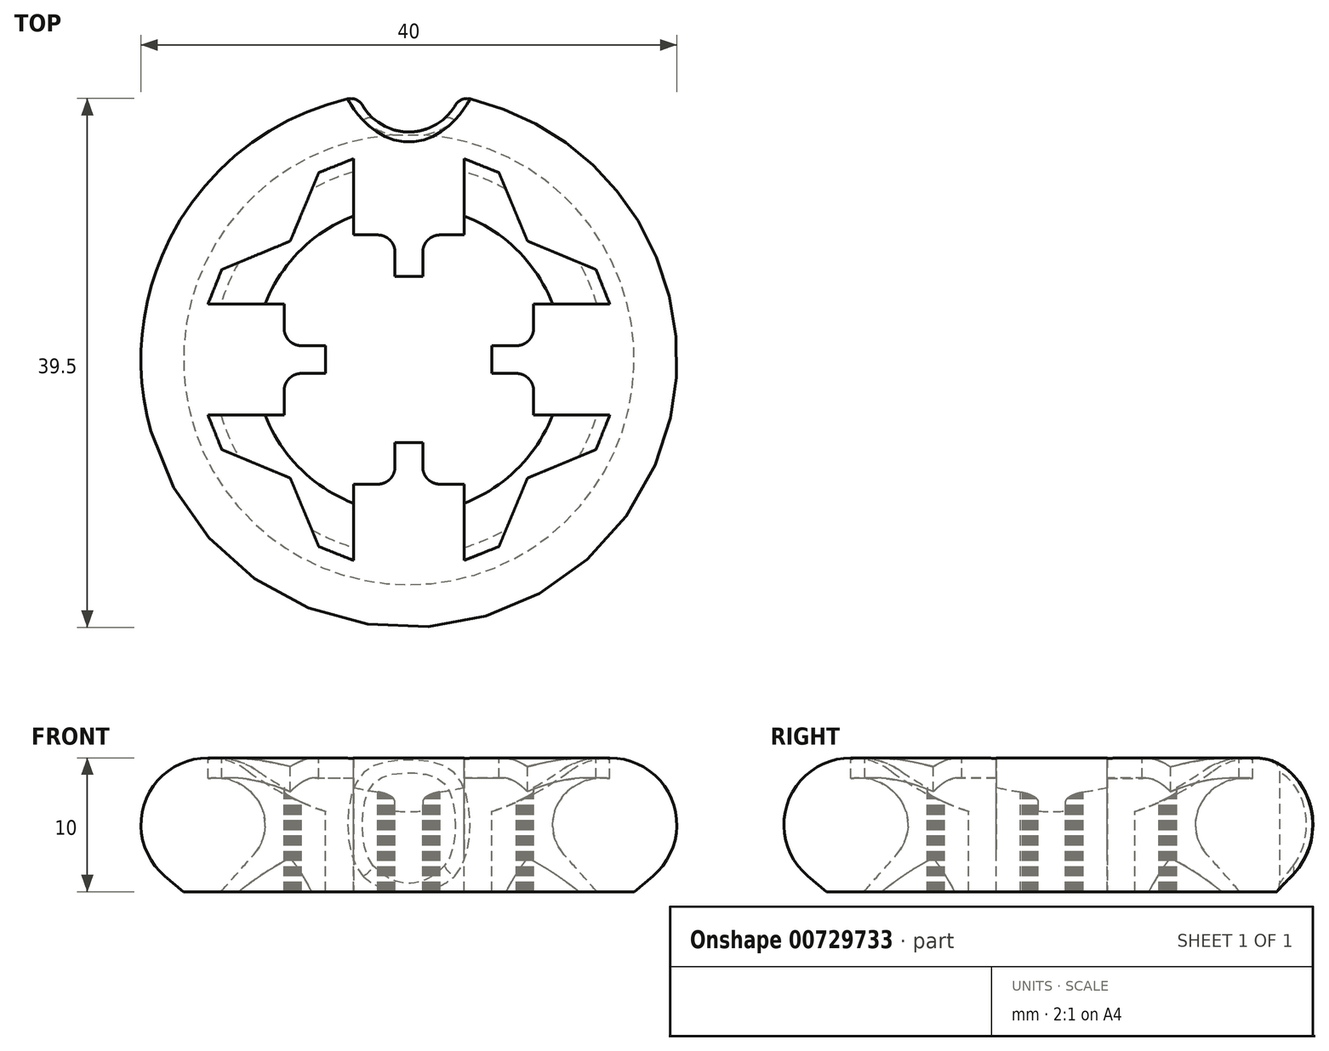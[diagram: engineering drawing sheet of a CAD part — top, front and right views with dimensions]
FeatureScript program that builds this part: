
annotation { "Feature Type Name" : "Feature", "Feature Type Description" : "" }
export const myFeature = defineFeature(function(context is Context, id is Id, definition is map)
    precondition{}
    {
        {
            var Q0;
            Q0=qCreatedBy(makeId("Front.planeOp"),FACE);
            var sketch = newSketch(context, id + "F0", { "sketchPlane" : qUnion([Q0])});
            skArc(sketch, "E0", {"start": v(-12, 9) * mm, "mid": v(-6.32, 6.03) * mm, "end": v(0, 5) * mm});
            skArc(sketch, "E1", {"start": v(-12, 9) * mm, "mid": v(-19.74, 6.58) * mm, "end": v(-15, 0) * mm});
            skLineSegment(sketch, "E2", {"start": v(0, 0) * mm, "end": v(-15, 0) * mm});
            skLineSegment(sketch, "E3", {"start": v(0, 0) * mm, "end": v(0, 5) * mm});
            skLineSegment(sketch, "E4", {"start": v(-18.21, 1.17) * mm, "end": v(-16.82, 0) * mm});
            skLineSegment(sketch, "E5", {"start": v(-16.82, 0) * mm, "end": v(-15, 0) * mm});
            skSolve(sketch);
        }
        {
            var Q0;
            Q0=qSketchRegion(id+"F0",true);
            var Q1;
            Q1=sQuery(id+"F0.wireOp",EDGE,"E3");
            revolve(context, id + "F1", {"surfaceOperationType" : NewSurfaceOperationType.NEW, "entities" : qUnion([Q0]), "axis" : qUnion([Q1]), "revolveType" : RevolveType.FULL});
        }
        {
            var Q0;
            Q0=qCreatedBy(makeId("Top.planeOp"),FACE);
            cPlane(context, id + "F2", {"entities" : qUnion([Q0]), "cplaneType" : CPlaneType.OFFSET, "offset" : 15 * mm, "width" : 150 * mm, "height" : 150 * mm});
        }
        {
            var Q0;
            Q0=qCreatedBy(id+"F2.planeOp",FACE);
            var sketch = newSketch(context, id + "F3", { "sketchPlane" : qUnion([Q0])});
            skLineSegment(sketch, "E6", {"start": v(9.31, -4.14) * mm, "end": v(9.31, -4.02) * mm});
            skLineSegment(sketch, "E7", {"start": v(9.31, -4.02) * mm, "end": v(9.31, -3.91) * mm});
            skLineSegment(sketch, "E8", {"start": v(9.31, -3.91) * mm, "end": v(9.31, -3.8) * mm});
            skLineSegment(sketch, "E9", {"start": v(9.31, -3.8) * mm, "end": v(9.31, -3.69) * mm});
            skLineSegment(sketch, "E10", {"start": v(9.31, -3.69) * mm, "end": v(9.31, -3.57) * mm});
            skLineSegment(sketch, "E11", {"start": v(9.31, -3.57) * mm, "end": v(9.31, -3.46) * mm});
            skLineSegment(sketch, "E12", {"start": v(9.31, -3.46) * mm, "end": v(9.31, -3.35) * mm});
            skLineSegment(sketch, "E13", {"start": v(9.31, -3.35) * mm, "end": v(9.31, -3.23) * mm});
            skLineSegment(sketch, "E14", {"start": v(9.31, -3.23) * mm, "end": v(9.31, -3.12) * mm});
            skLineSegment(sketch, "E15", {"start": v(9.31, -3.12) * mm, "end": v(9.31, -3) * mm});
            skLineSegment(sketch, "E16", {"start": v(9.31, -3) * mm, "end": v(9.31, -2.9) * mm});
            skLineSegment(sketch, "E17", {"start": v(9.31, -2.9) * mm, "end": v(9.31, -2.78) * mm});
            skLineSegment(sketch, "E18", {"start": v(9.31, -2.78) * mm, "end": v(9.31, -2.67) * mm});
            skLineSegment(sketch, "E19", {"start": v(9.31, -2.67) * mm, "end": v(9.31, -2.55) * mm});
            skLineSegment(sketch, "E20", {"start": v(9.31, -2.55) * mm, "end": v(9.31, -2.44) * mm});
            skLineSegment(sketch, "E21", {"start": v(9.31, -2.44) * mm, "end": v(9.31, -2.33) * mm});
            skLineSegment(sketch, "E22", {"start": v(9.31, -2.33) * mm, "end": v(9.3, -2.2) * mm});
            skLineSegment(sketch, "E23", {"start": v(9.3, -2.2) * mm, "end": v(9.28, -2.07) * mm});
            skLineSegment(sketch, "E24", {"start": v(9.28, -2.07) * mm, "end": v(9.25, -1.94) * mm});
            skLineSegment(sketch, "E25", {"start": v(9.25, -1.94) * mm, "end": v(9.2, -1.82) * mm});
            skLineSegment(sketch, "E26", {"start": v(9.2, -1.82) * mm, "end": v(9.15, -1.71) * mm});
            skLineSegment(sketch, "E27", {"start": v(9.15, -1.71) * mm, "end": v(9.09, -1.6) * mm});
            skLineSegment(sketch, "E28", {"start": v(9.09, -1.6) * mm, "end": v(9.02, -1.5) * mm});
            skLineSegment(sketch, "E29", {"start": v(9.02, -1.5) * mm, "end": v(8.93, -1.41) * mm});
            skLineSegment(sketch, "E30", {"start": v(8.93, -1.41) * mm, "end": v(8.84, -1.33) * mm});
            skLineSegment(sketch, "E31", {"start": v(8.84, -1.33) * mm, "end": v(8.74, -1.26) * mm});
            skLineSegment(sketch, "E32", {"start": v(8.74, -1.26) * mm, "end": v(8.63, -1.2) * mm});
            skLineSegment(sketch, "E33", {"start": v(8.63, -1.2) * mm, "end": v(8.52, -1.14) * mm});
            skLineSegment(sketch, "E34", {"start": v(8.52, -1.14) * mm, "end": v(8.4, -1.1) * mm});
            skLineSegment(sketch, "E35", {"start": v(8.4, -1.1) * mm, "end": v(8.28, -1.06) * mm});
            skLineSegment(sketch, "E36", {"start": v(8.28, -1.06) * mm, "end": v(8.15, -1.04) * mm});
            skLineSegment(sketch, "E37", {"start": v(8.15, -1.04) * mm, "end": v(8.02, -1.03) * mm});
            skLineSegment(sketch, "E38", {"start": v(8.02, -1.03) * mm, "end": v(7.9, -1.03) * mm});
            skLineSegment(sketch, "E39", {"start": v(7.9, -1.03) * mm, "end": v(7.8, -1.03) * mm});
            skLineSegment(sketch, "E40", {"start": v(7.8, -1.03) * mm, "end": v(7.68, -1.03) * mm});
            skLineSegment(sketch, "E41", {"start": v(7.68, -1.03) * mm, "end": v(7.56, -1.03) * mm});
            skLineSegment(sketch, "E42", {"start": v(7.56, -1.03) * mm, "end": v(7.45, -1.03) * mm});
            skLineSegment(sketch, "E43", {"start": v(7.45, -1.03) * mm, "end": v(7.34, -1.03) * mm});
            skLineSegment(sketch, "E44", {"start": v(7.34, -1.03) * mm, "end": v(7.23, -1.03) * mm});
            skLineSegment(sketch, "E45", {"start": v(7.23, -1.03) * mm, "end": v(7.11, -1.03) * mm});
            skLineSegment(sketch, "E46", {"start": v(7.11, -1.03) * mm, "end": v(7, -1.03) * mm});
            skLineSegment(sketch, "E47", {"start": v(7, -1.03) * mm, "end": v(6.89, -1.03) * mm});
            skLineSegment(sketch, "E48", {"start": v(6.89, -1.03) * mm, "end": v(6.77, -1.03) * mm});
            skLineSegment(sketch, "E49", {"start": v(6.77, -1.03) * mm, "end": v(6.66, -1.03) * mm});
            skLineSegment(sketch, "E50", {"start": v(6.66, -1.03) * mm, "end": v(6.55, -1.03) * mm});
            skLineSegment(sketch, "E51", {"start": v(6.55, -1.03) * mm, "end": v(6.43, -1.03) * mm});
            skLineSegment(sketch, "E52", {"start": v(6.43, -1.03) * mm, "end": v(6.32, -1.03) * mm});
            skLineSegment(sketch, "E53", {"start": v(6.32, -1.03) * mm, "end": v(6.2, -1.03) * mm});
            skLineSegment(sketch, "E54", {"start": v(6.2, -1.03) * mm, "end": v(6.2, -0.97) * mm});
            skLineSegment(sketch, "E55", {"start": v(6.2, -0.97) * mm, "end": v(6.2, -0.9) * mm});
            skLineSegment(sketch, "E56", {"start": v(6.2, -0.9) * mm, "end": v(6.2, -0.84) * mm});
            skLineSegment(sketch, "E57", {"start": v(6.2, -0.84) * mm, "end": v(6.2, -0.78) * mm});
            skLineSegment(sketch, "E58", {"start": v(6.2, -0.78) * mm, "end": v(6.2, -0.71) * mm});
            skLineSegment(sketch, "E59", {"start": v(6.2, -0.71) * mm, "end": v(6.2, -0.65) * mm});
            skLineSegment(sketch, "E60", {"start": v(6.2, -0.65) * mm, "end": v(6.2, -0.58) * mm});
            skLineSegment(sketch, "E61", {"start": v(6.2, -0.58) * mm, "end": v(6.2, -0.52) * mm});
            skLineSegment(sketch, "E62", {"start": v(6.2, -0.52) * mm, "end": v(6.2, -0.45) * mm});
            skLineSegment(sketch, "E63", {"start": v(6.2, -0.45) * mm, "end": v(6.2, -0.39) * mm});
            skLineSegment(sketch, "E64", {"start": v(6.2, -0.39) * mm, "end": v(6.2, -0.32) * mm});
            skLineSegment(sketch, "E65", {"start": v(6.2, -0.32) * mm, "end": v(6.2, -0.26) * mm});
            skLineSegment(sketch, "E66", {"start": v(6.2, -0.26) * mm, "end": v(6.2, -0.2) * mm});
            skLineSegment(sketch, "E67", {"start": v(6.2, -0.2) * mm, "end": v(6.2, -0.13) * mm});
            skLineSegment(sketch, "E68", {"start": v(6.2, -0.13) * mm, "end": v(6.2, -0.06) * mm});
            skLineSegment(sketch, "E69", {"start": v(6.2, -0.06) * mm, "end": v(6.2, 0) * mm});
            skLineSegment(sketch, "E70", {"start": v(6.2, 0) * mm, "end": v(6.2, 0.06) * mm});
            skLineSegment(sketch, "E71", {"start": v(6.2, 0.06) * mm, "end": v(6.2, 0.13) * mm});
            skLineSegment(sketch, "E72", {"start": v(6.2, 0.13) * mm, "end": v(6.2, 0.2) * mm});
            skLineSegment(sketch, "E73", {"start": v(6.2, 0.2) * mm, "end": v(6.2, 0.26) * mm});
            skLineSegment(sketch, "E74", {"start": v(6.2, 0.26) * mm, "end": v(6.2, 0.32) * mm});
            skLineSegment(sketch, "E75", {"start": v(6.2, 0.32) * mm, "end": v(6.2, 0.39) * mm});
            skLineSegment(sketch, "E76", {"start": v(6.2, 0.39) * mm, "end": v(6.2, 0.45) * mm});
            skLineSegment(sketch, "E77", {"start": v(6.2, 0.45) * mm, "end": v(6.2, 0.52) * mm});
            skLineSegment(sketch, "E78", {"start": v(6.2, 0.52) * mm, "end": v(6.2, 0.58) * mm});
            skLineSegment(sketch, "E79", {"start": v(6.2, 0.58) * mm, "end": v(6.2, 0.65) * mm});
            skLineSegment(sketch, "E80", {"start": v(6.2, 0.65) * mm, "end": v(6.2, 0.71) * mm});
            skLineSegment(sketch, "E81", {"start": v(6.2, 0.71) * mm, "end": v(6.2, 0.78) * mm});
            skLineSegment(sketch, "E82", {"start": v(6.2, 0.78) * mm, "end": v(6.2, 0.84) * mm});
            skLineSegment(sketch, "E83", {"start": v(6.2, 0.84) * mm, "end": v(6.2, 0.9) * mm});
            skLineSegment(sketch, "E84", {"start": v(6.2, 0.9) * mm, "end": v(6.2, 0.97) * mm});
            skLineSegment(sketch, "E85", {"start": v(6.2, 0.97) * mm, "end": v(6.2, 1.03) * mm});
            skLineSegment(sketch, "E86", {"start": v(6.2, 1.03) * mm, "end": v(6.32, 1.03) * mm});
            skLineSegment(sketch, "E87", {"start": v(6.32, 1.03) * mm, "end": v(6.43, 1.03) * mm});
            skLineSegment(sketch, "E88", {"start": v(6.43, 1.03) * mm, "end": v(6.55, 1.03) * mm});
            skLineSegment(sketch, "E89", {"start": v(6.55, 1.03) * mm, "end": v(6.66, 1.03) * mm});
            skLineSegment(sketch, "E90", {"start": v(6.66, 1.03) * mm, "end": v(6.77, 1.03) * mm});
            skLineSegment(sketch, "E91", {"start": v(6.77, 1.03) * mm, "end": v(6.89, 1.03) * mm});
            skLineSegment(sketch, "E92", {"start": v(6.89, 1.03) * mm, "end": v(7, 1.03) * mm});
            skLineSegment(sketch, "E93", {"start": v(7, 1.03) * mm, "end": v(7.11, 1.03) * mm});
            skLineSegment(sketch, "E94", {"start": v(7.11, 1.03) * mm, "end": v(7.23, 1.03) * mm});
            skLineSegment(sketch, "E95", {"start": v(7.23, 1.03) * mm, "end": v(7.34, 1.03) * mm});
            skLineSegment(sketch, "E96", {"start": v(7.34, 1.03) * mm, "end": v(7.45, 1.03) * mm});
            skLineSegment(sketch, "E97", {"start": v(7.45, 1.03) * mm, "end": v(7.56, 1.03) * mm});
            skLineSegment(sketch, "E98", {"start": v(7.56, 1.03) * mm, "end": v(7.68, 1.03) * mm});
            skLineSegment(sketch, "E99", {"start": v(7.68, 1.03) * mm, "end": v(7.8, 1.03) * mm});
            skLineSegment(sketch, "E100", {"start": v(7.8, 1.03) * mm, "end": v(7.9, 1.03) * mm});
            skLineSegment(sketch, "E101", {"start": v(7.9, 1.03) * mm, "end": v(8.02, 1.03) * mm});
            skLineSegment(sketch, "E102", {"start": v(8.02, 1.03) * mm, "end": v(8.15, 1.04) * mm});
            skLineSegment(sketch, "E103", {"start": v(8.15, 1.04) * mm, "end": v(8.28, 1.06) * mm});
            skLineSegment(sketch, "E104", {"start": v(8.28, 1.06) * mm, "end": v(8.4, 1.1) * mm});
            skLineSegment(sketch, "E105", {"start": v(8.4, 1.1) * mm, "end": v(8.52, 1.14) * mm});
            skLineSegment(sketch, "E106", {"start": v(8.52, 1.14) * mm, "end": v(8.63, 1.2) * mm});
            skLineSegment(sketch, "E107", {"start": v(8.63, 1.2) * mm, "end": v(8.74, 1.26) * mm});
            skLineSegment(sketch, "E108", {"start": v(8.74, 1.26) * mm, "end": v(8.84, 1.33) * mm});
            skLineSegment(sketch, "E109", {"start": v(8.84, 1.33) * mm, "end": v(8.93, 1.41) * mm});
            skLineSegment(sketch, "E110", {"start": v(8.93, 1.41) * mm, "end": v(9.02, 1.5) * mm});
            skLineSegment(sketch, "E111", {"start": v(9.02, 1.5) * mm, "end": v(9.09, 1.6) * mm});
            skLineSegment(sketch, "E112", {"start": v(9.09, 1.6) * mm, "end": v(9.15, 1.71) * mm});
            skLineSegment(sketch, "E113", {"start": v(9.15, 1.71) * mm, "end": v(9.2, 1.82) * mm});
            skLineSegment(sketch, "E114", {"start": v(9.2, 1.82) * mm, "end": v(9.25, 1.94) * mm});
            skLineSegment(sketch, "E115", {"start": v(9.25, 1.94) * mm, "end": v(9.28, 2.07) * mm});
            skLineSegment(sketch, "E116", {"start": v(9.28, 2.07) * mm, "end": v(9.3, 2.2) * mm});
            skLineSegment(sketch, "E117", {"start": v(9.3, 2.2) * mm, "end": v(9.31, 2.33) * mm});
            skLineSegment(sketch, "E118", {"start": v(9.31, 2.33) * mm, "end": v(9.31, 2.44) * mm});
            skLineSegment(sketch, "E119", {"start": v(9.31, 2.44) * mm, "end": v(9.31, 2.55) * mm});
            skLineSegment(sketch, "E120", {"start": v(9.31, 2.55) * mm, "end": v(9.31, 2.67) * mm});
            skLineSegment(sketch, "E121", {"start": v(9.31, 2.67) * mm, "end": v(9.31, 2.78) * mm});
            skLineSegment(sketch, "E122", {"start": v(9.31, 2.78) * mm, "end": v(9.31, 2.9) * mm});
            skLineSegment(sketch, "E123", {"start": v(9.31, 2.9) * mm, "end": v(9.31, 3) * mm});
            skLineSegment(sketch, "E124", {"start": v(9.31, 3) * mm, "end": v(9.31, 3.12) * mm});
            skLineSegment(sketch, "E125", {"start": v(9.31, 3.12) * mm, "end": v(9.31, 3.23) * mm});
            skLineSegment(sketch, "E126", {"start": v(9.31, 3.23) * mm, "end": v(9.31, 3.35) * mm});
            skLineSegment(sketch, "E127", {"start": v(9.31, 3.35) * mm, "end": v(9.31, 3.46) * mm});
            skLineSegment(sketch, "E128", {"start": v(9.31, 3.46) * mm, "end": v(9.31, 3.57) * mm});
            skLineSegment(sketch, "E129", {"start": v(9.31, 3.57) * mm, "end": v(9.31, 3.69) * mm});
            skLineSegment(sketch, "E130", {"start": v(9.31, 3.69) * mm, "end": v(9.31, 3.8) * mm});
            skLineSegment(sketch, "E131", {"start": v(9.31, 3.8) * mm, "end": v(9.31, 3.91) * mm});
            skLineSegment(sketch, "E132", {"start": v(9.31, 3.91) * mm, "end": v(9.31, 4.02) * mm});
            skLineSegment(sketch, "E133", {"start": v(9.31, 4.02) * mm, "end": v(9.31, 4.14) * mm});
            skLineSegment(sketch, "E134", {"start": v(9.31, 4.14) * mm, "end": v(9.44, 4.14) * mm});
            skLineSegment(sketch, "E135", {"start": v(9.44, 4.14) * mm, "end": v(9.57, 4.14) * mm});
            skLineSegment(sketch, "E136", {"start": v(9.57, 4.14) * mm, "end": v(9.7, 4.14) * mm});
            skLineSegment(sketch, "E137", {"start": v(9.7, 4.14) * mm, "end": v(9.83, 4.14) * mm});
            skLineSegment(sketch, "E138", {"start": v(9.83, 4.14) * mm, "end": v(9.96, 4.14) * mm});
            skLineSegment(sketch, "E139", {"start": v(9.96, 4.14) * mm, "end": v(10.09, 4.14) * mm});
            skLineSegment(sketch, "E140", {"start": v(10.09, 4.14) * mm, "end": v(10.22, 4.14) * mm});
            skLineSegment(sketch, "E141", {"start": v(10.22, 4.14) * mm, "end": v(10.34, 4.14) * mm});
            skLineSegment(sketch, "E142", {"start": v(10.34, 4.14) * mm, "end": v(10.47, 4.14) * mm});
            skLineSegment(sketch, "E143", {"start": v(10.47, 4.14) * mm, "end": v(10.6, 4.14) * mm});
            skLineSegment(sketch, "E144", {"start": v(10.6, 4.14) * mm, "end": v(10.73, 4.14) * mm});
            skLineSegment(sketch, "E145", {"start": v(10.73, 4.14) * mm, "end": v(10.86, 4.14) * mm});
            skLineSegment(sketch, "E146", {"start": v(10.86, 4.14) * mm, "end": v(11, 4.14) * mm});
            skLineSegment(sketch, "E147", {"start": v(11, 4.14) * mm, "end": v(11.12, 4.14) * mm});
            skLineSegment(sketch, "E148", {"start": v(11.12, 4.14) * mm, "end": v(11.25, 4.14) * mm});
            skLineSegment(sketch, "E149", {"start": v(11.25, 4.14) * mm, "end": v(11.38, 4.14) * mm});
            skLineSegment(sketch, "E150", {"start": v(11.38, 4.14) * mm, "end": v(11.6, 4.14) * mm});
            skLineSegment(sketch, "E151", {"start": v(11.6, 4.14) * mm, "end": v(11.83, 4.14) * mm});
            skLineSegment(sketch, "E152", {"start": v(11.83, 4.14) * mm, "end": v(12.06, 4.14) * mm});
            skLineSegment(sketch, "E153", {"start": v(12.06, 4.14) * mm, "end": v(12.28, 4.14) * mm});
            skLineSegment(sketch, "E154", {"start": v(12.28, 4.14) * mm, "end": v(12.51, 4.14) * mm});
            skLineSegment(sketch, "E155", {"start": v(12.51, 4.14) * mm, "end": v(12.74, 4.14) * mm});
            skLineSegment(sketch, "E156", {"start": v(12.74, 4.14) * mm, "end": v(12.96, 4.14) * mm});
            skLineSegment(sketch, "E157", {"start": v(12.96, 4.14) * mm, "end": v(13.19, 4.14) * mm});
            skLineSegment(sketch, "E158", {"start": v(13.19, 4.14) * mm, "end": v(13.42, 4.14) * mm});
            skLineSegment(sketch, "E159", {"start": v(13.42, 4.14) * mm, "end": v(13.64, 4.14) * mm});
            skLineSegment(sketch, "E160", {"start": v(13.64, 4.14) * mm, "end": v(13.87, 4.14) * mm});
            skLineSegment(sketch, "E161", {"start": v(13.87, 4.14) * mm, "end": v(14.1, 4.14) * mm});
            skLineSegment(sketch, "E162", {"start": v(14.1, 4.14) * mm, "end": v(14.32, 4.14) * mm});
            skLineSegment(sketch, "E163", {"start": v(14.32, 4.14) * mm, "end": v(14.55, 4.14) * mm});
            skLineSegment(sketch, "E164", {"start": v(14.55, 4.14) * mm, "end": v(14.77, 4.14) * mm});
            skLineSegment(sketch, "E165", {"start": v(14.77, 4.14) * mm, "end": v(15, 4.14) * mm});
            skLineSegment(sketch, "E166", {"start": v(15, 4.14) * mm, "end": v(14.95, 4.27) * mm});
            skLineSegment(sketch, "E167", {"start": v(14.95, 4.27) * mm, "end": v(14.9, 4.4) * mm});
            skLineSegment(sketch, "E168", {"start": v(14.9, 4.4) * mm, "end": v(14.84, 4.53) * mm});
            skLineSegment(sketch, "E169", {"start": v(14.84, 4.53) * mm, "end": v(14.8, 4.66) * mm});
            skLineSegment(sketch, "E170", {"start": v(14.8, 4.66) * mm, "end": v(14.74, 4.78) * mm});
            skLineSegment(sketch, "E171", {"start": v(14.74, 4.78) * mm, "end": v(14.69, 4.91) * mm});
            skLineSegment(sketch, "E172", {"start": v(14.69, 4.91) * mm, "end": v(14.64, 5.04) * mm});
            skLineSegment(sketch, "E173", {"start": v(14.64, 5.04) * mm, "end": v(14.59, 5.17) * mm});
            skLineSegment(sketch, "E174", {"start": v(14.59, 5.17) * mm, "end": v(14.53, 5.3) * mm});
            skLineSegment(sketch, "E175", {"start": v(14.53, 5.3) * mm, "end": v(14.48, 5.43) * mm});
            skLineSegment(sketch, "E176", {"start": v(14.48, 5.43) * mm, "end": v(14.43, 5.56) * mm});
            skLineSegment(sketch, "E177", {"start": v(14.43, 5.56) * mm, "end": v(14.38, 5.69) * mm});
            skLineSegment(sketch, "E178", {"start": v(14.38, 5.69) * mm, "end": v(14.33, 5.82) * mm});
            skLineSegment(sketch, "E179", {"start": v(14.33, 5.82) * mm, "end": v(14.28, 5.95) * mm});
            skLineSegment(sketch, "E180", {"start": v(14.28, 5.95) * mm, "end": v(14.22, 6.08) * mm});
            skLineSegment(sketch, "E181", {"start": v(14.22, 6.08) * mm, "end": v(14.17, 6.2) * mm});
            skLineSegment(sketch, "E182", {"start": v(14.17, 6.2) * mm, "end": v(14.16, 6.24) * mm});
            skLineSegment(sketch, "E183", {"start": v(14.16, 6.24) * mm, "end": v(14.15, 6.27) * mm});
            skLineSegment(sketch, "E184", {"start": v(14.15, 6.27) * mm, "end": v(14.13, 6.3) * mm});
            skLineSegment(sketch, "E185", {"start": v(14.13, 6.3) * mm, "end": v(14.12, 6.34) * mm});
            skLineSegment(sketch, "E186", {"start": v(14.12, 6.34) * mm, "end": v(14.1, 6.37) * mm});
            skLineSegment(sketch, "E187", {"start": v(14.1, 6.37) * mm, "end": v(14.1, 6.4) * mm});
            skLineSegment(sketch, "E188", {"start": v(14.1, 6.4) * mm, "end": v(14.08, 6.43) * mm});
            skLineSegment(sketch, "E189", {"start": v(14.08, 6.43) * mm, "end": v(14.07, 6.47) * mm});
            skLineSegment(sketch, "E190", {"start": v(14.07, 6.47) * mm, "end": v(14.06, 6.5) * mm});
            skLineSegment(sketch, "E191", {"start": v(14.06, 6.5) * mm, "end": v(14.04, 6.53) * mm});
            skLineSegment(sketch, "E192", {"start": v(14.04, 6.53) * mm, "end": v(14.03, 6.56) * mm});
            skLineSegment(sketch, "E193", {"start": v(14.03, 6.56) * mm, "end": v(14.02, 6.6) * mm});
            skLineSegment(sketch, "E194", {"start": v(14.02, 6.6) * mm, "end": v(14, 6.63) * mm});
            skLineSegment(sketch, "E195", {"start": v(14, 6.63) * mm, "end": v(14, 6.66) * mm});
            skLineSegment(sketch, "E196", {"start": v(14, 6.66) * mm, "end": v(13.98, 6.7) * mm});
            skLineSegment(sketch, "E197", {"start": v(13.98, 6.7) * mm, "end": v(13.97, 6.72) * mm});
            skLineSegment(sketch, "E198", {"start": v(13.97, 6.72) * mm, "end": v(13.65, 6.86) * mm});
            skLineSegment(sketch, "E199", {"start": v(13.65, 6.86) * mm, "end": v(13.33, 7) * mm});
            skLineSegment(sketch, "E200", {"start": v(13.33, 7) * mm, "end": v(13, 7.12) * mm});
            skLineSegment(sketch, "E201", {"start": v(13, 7.12) * mm, "end": v(12.69, 7.26) * mm});
            skLineSegment(sketch, "E202", {"start": v(12.69, 7.26) * mm, "end": v(12.37, 7.39) * mm});
            skLineSegment(sketch, "E203", {"start": v(12.37, 7.39) * mm, "end": v(12.05, 7.52) * mm});
            skLineSegment(sketch, "E204", {"start": v(12.05, 7.52) * mm, "end": v(11.73, 7.66) * mm});
            skLineSegment(sketch, "E205", {"start": v(11.73, 7.66) * mm, "end": v(11.4, 7.79) * mm});
            skLineSegment(sketch, "E206", {"start": v(11.4, 7.79) * mm, "end": v(11.1, 7.92) * mm});
            skLineSegment(sketch, "E207", {"start": v(11.1, 7.92) * mm, "end": v(10.77, 8.06) * mm});
            skLineSegment(sketch, "E208", {"start": v(10.77, 8.06) * mm, "end": v(10.45, 8.19) * mm});
            skLineSegment(sketch, "E209", {"start": v(10.45, 8.19) * mm, "end": v(10.13, 8.32) * mm});
            skLineSegment(sketch, "E210", {"start": v(10.13, 8.32) * mm, "end": v(9.81, 8.45) * mm});
            skLineSegment(sketch, "E211", {"start": v(9.81, 8.45) * mm, "end": v(9.5, 8.59) * mm});
            skLineSegment(sketch, "E212", {"start": v(9.5, 8.59) * mm, "end": v(9.17, 8.72) * mm});
            skLineSegment(sketch, "E213", {"start": v(9.17, 8.72) * mm, "end": v(8.85, 8.85) * mm});
            skLineSegment(sketch, "E214", {"start": v(8.85, 8.85) * mm, "end": v(8.72, 9.17) * mm});
            skLineSegment(sketch, "E215", {"start": v(8.72, 9.17) * mm, "end": v(8.59, 9.5) * mm});
            skLineSegment(sketch, "E216", {"start": v(8.59, 9.5) * mm, "end": v(8.45, 9.81) * mm});
            skLineSegment(sketch, "E217", {"start": v(8.45, 9.81) * mm, "end": v(8.32, 10.13) * mm});
            skLineSegment(sketch, "E218", {"start": v(8.32, 10.13) * mm, "end": v(8.19, 10.45) * mm});
            skLineSegment(sketch, "E219", {"start": v(8.19, 10.45) * mm, "end": v(8.06, 10.77) * mm});
            skLineSegment(sketch, "E220", {"start": v(8.06, 10.77) * mm, "end": v(7.92, 11.1) * mm});
            skLineSegment(sketch, "E221", {"start": v(7.92, 11.1) * mm, "end": v(7.79, 11.4) * mm});
            skLineSegment(sketch, "E222", {"start": v(7.79, 11.4) * mm, "end": v(7.66, 11.73) * mm});
            skLineSegment(sketch, "E223", {"start": v(7.66, 11.73) * mm, "end": v(7.52, 12.05) * mm});
            skLineSegment(sketch, "E224", {"start": v(7.52, 12.05) * mm, "end": v(7.39, 12.37) * mm});
            skLineSegment(sketch, "E225", {"start": v(7.39, 12.37) * mm, "end": v(7.26, 12.69) * mm});
            skLineSegment(sketch, "E226", {"start": v(7.26, 12.69) * mm, "end": v(7.12, 13) * mm});
            skLineSegment(sketch, "E227", {"start": v(7.12, 13) * mm, "end": v(7, 13.33) * mm});
            skLineSegment(sketch, "E228", {"start": v(7, 13.33) * mm, "end": v(6.86, 13.65) * mm});
            skLineSegment(sketch, "E229", {"start": v(6.86, 13.65) * mm, "end": v(6.72, 13.97) * mm});
            skLineSegment(sketch, "E230", {"start": v(6.72, 13.97) * mm, "end": v(6.7, 13.98) * mm});
            skLineSegment(sketch, "E231", {"start": v(6.7, 13.98) * mm, "end": v(6.66, 14) * mm});
            skLineSegment(sketch, "E232", {"start": v(6.66, 14) * mm, "end": v(6.63, 14) * mm});
            skLineSegment(sketch, "E233", {"start": v(6.63, 14) * mm, "end": v(6.6, 14.02) * mm});
            skLineSegment(sketch, "E234", {"start": v(6.6, 14.02) * mm, "end": v(6.56, 14.03) * mm});
            skLineSegment(sketch, "E235", {"start": v(6.56, 14.03) * mm, "end": v(6.53, 14.04) * mm});
            skLineSegment(sketch, "E236", {"start": v(6.53, 14.04) * mm, "end": v(6.5, 14.06) * mm});
            skLineSegment(sketch, "E237", {"start": v(6.5, 14.06) * mm, "end": v(6.47, 14.07) * mm});
            skLineSegment(sketch, "E238", {"start": v(6.47, 14.07) * mm, "end": v(6.43, 14.08) * mm});
            skLineSegment(sketch, "E239", {"start": v(6.43, 14.08) * mm, "end": v(6.4, 14.1) * mm});
            skLineSegment(sketch, "E240", {"start": v(6.4, 14.1) * mm, "end": v(6.37, 14.1) * mm});
            skLineSegment(sketch, "E241", {"start": v(6.37, 14.1) * mm, "end": v(6.34, 14.12) * mm});
            skLineSegment(sketch, "E242", {"start": v(6.34, 14.12) * mm, "end": v(6.3, 14.13) * mm});
            skLineSegment(sketch, "E243", {"start": v(6.3, 14.13) * mm, "end": v(6.27, 14.15) * mm});
            skLineSegment(sketch, "E244", {"start": v(6.27, 14.15) * mm, "end": v(6.24, 14.16) * mm});
            skLineSegment(sketch, "E245", {"start": v(6.24, 14.16) * mm, "end": v(6.2, 14.17) * mm});
            skLineSegment(sketch, "E246", {"start": v(6.2, 14.17) * mm, "end": v(6.08, 14.22) * mm});
            skLineSegment(sketch, "E247", {"start": v(6.08, 14.22) * mm, "end": v(5.95, 14.28) * mm});
            skLineSegment(sketch, "E248", {"start": v(5.95, 14.28) * mm, "end": v(5.82, 14.33) * mm});
            skLineSegment(sketch, "E249", {"start": v(5.82, 14.33) * mm, "end": v(5.69, 14.38) * mm});
            skLineSegment(sketch, "E250", {"start": v(5.69, 14.38) * mm, "end": v(5.56, 14.43) * mm});
            skLineSegment(sketch, "E251", {"start": v(5.56, 14.43) * mm, "end": v(5.43, 14.48) * mm});
            skLineSegment(sketch, "E252", {"start": v(5.43, 14.48) * mm, "end": v(5.3, 14.53) * mm});
            skLineSegment(sketch, "E253", {"start": v(5.3, 14.53) * mm, "end": v(5.17, 14.59) * mm});
            skLineSegment(sketch, "E254", {"start": v(5.17, 14.59) * mm, "end": v(5.04, 14.64) * mm});
            skLineSegment(sketch, "E255", {"start": v(5.04, 14.64) * mm, "end": v(4.91, 14.69) * mm});
            skLineSegment(sketch, "E256", {"start": v(4.91, 14.69) * mm, "end": v(4.78, 14.74) * mm});
            skLineSegment(sketch, "E257", {"start": v(4.78, 14.74) * mm, "end": v(4.66, 14.8) * mm});
            skLineSegment(sketch, "E258", {"start": v(4.66, 14.8) * mm, "end": v(4.53, 14.84) * mm});
            skLineSegment(sketch, "E259", {"start": v(4.53, 14.84) * mm, "end": v(4.4, 14.9) * mm});
            skLineSegment(sketch, "E260", {"start": v(4.4, 14.9) * mm, "end": v(4.27, 14.95) * mm});
            skLineSegment(sketch, "E261", {"start": v(4.27, 14.95) * mm, "end": v(4.14, 15) * mm});
            skLineSegment(sketch, "E262", {"start": v(4.14, 15) * mm, "end": v(4.14, 14.77) * mm});
            skLineSegment(sketch, "E263", {"start": v(4.14, 14.77) * mm, "end": v(4.14, 14.55) * mm});
            skLineSegment(sketch, "E264", {"start": v(4.14, 14.55) * mm, "end": v(4.14, 14.32) * mm});
            skLineSegment(sketch, "E265", {"start": v(4.14, 14.32) * mm, "end": v(4.14, 14.1) * mm});
            skLineSegment(sketch, "E266", {"start": v(4.14, 14.1) * mm, "end": v(4.14, 13.87) * mm});
            skLineSegment(sketch, "E267", {"start": v(4.14, 13.87) * mm, "end": v(4.14, 13.64) * mm});
            skLineSegment(sketch, "E268", {"start": v(4.14, 13.64) * mm, "end": v(4.14, 13.42) * mm});
            skLineSegment(sketch, "E269", {"start": v(4.14, 13.42) * mm, "end": v(4.14, 13.19) * mm});
            skLineSegment(sketch, "E270", {"start": v(4.14, 13.19) * mm, "end": v(4.14, 12.96) * mm});
            skLineSegment(sketch, "E271", {"start": v(4.14, 12.96) * mm, "end": v(4.14, 12.74) * mm});
            skLineSegment(sketch, "E272", {"start": v(4.14, 12.74) * mm, "end": v(4.14, 12.51) * mm});
            skLineSegment(sketch, "E273", {"start": v(4.14, 12.51) * mm, "end": v(4.14, 12.28) * mm});
            skLineSegment(sketch, "E274", {"start": v(4.14, 12.28) * mm, "end": v(4.14, 12.06) * mm});
            skLineSegment(sketch, "E275", {"start": v(4.14, 12.06) * mm, "end": v(4.14, 11.83) * mm});
            skLineSegment(sketch, "E276", {"start": v(4.14, 11.83) * mm, "end": v(4.14, 11.6) * mm});
            skLineSegment(sketch, "E277", {"start": v(4.14, 11.6) * mm, "end": v(4.14, 11.38) * mm});
            skLineSegment(sketch, "E278", {"start": v(4.14, 11.38) * mm, "end": v(4.14, 11.25) * mm});
            skLineSegment(sketch, "E279", {"start": v(4.14, 11.25) * mm, "end": v(4.14, 11.12) * mm});
            skLineSegment(sketch, "E280", {"start": v(4.14, 11.12) * mm, "end": v(4.14, 11) * mm});
            skLineSegment(sketch, "E281", {"start": v(4.14, 11) * mm, "end": v(4.14, 10.86) * mm});
            skLineSegment(sketch, "E282", {"start": v(4.14, 10.86) * mm, "end": v(4.14, 10.73) * mm});
            skLineSegment(sketch, "E283", {"start": v(4.14, 10.73) * mm, "end": v(4.14, 10.6) * mm});
            skLineSegment(sketch, "E284", {"start": v(4.14, 10.6) * mm, "end": v(4.14, 10.47) * mm});
            skLineSegment(sketch, "E285", {"start": v(4.14, 10.47) * mm, "end": v(4.14, 10.34) * mm});
            skLineSegment(sketch, "E286", {"start": v(4.14, 10.34) * mm, "end": v(4.14, 10.22) * mm});
            skLineSegment(sketch, "E287", {"start": v(4.14, 10.22) * mm, "end": v(4.14, 10.09) * mm});
            skLineSegment(sketch, "E288", {"start": v(4.14, 10.09) * mm, "end": v(4.14, 9.96) * mm});
            skLineSegment(sketch, "E289", {"start": v(4.14, 9.96) * mm, "end": v(4.14, 9.83) * mm});
            skLineSegment(sketch, "E290", {"start": v(4.14, 9.83) * mm, "end": v(4.14, 9.7) * mm});
            skLineSegment(sketch, "E291", {"start": v(4.14, 9.7) * mm, "end": v(4.14, 9.57) * mm});
            skLineSegment(sketch, "E292", {"start": v(4.14, 9.57) * mm, "end": v(4.14, 9.44) * mm});
            skLineSegment(sketch, "E293", {"start": v(4.14, 9.44) * mm, "end": v(4.14, 9.31) * mm});
            skLineSegment(sketch, "E294", {"start": v(4.14, 9.31) * mm, "end": v(4.02, 9.31) * mm});
            skLineSegment(sketch, "E295", {"start": v(4.02, 9.31) * mm, "end": v(3.91, 9.31) * mm});
            skLineSegment(sketch, "E296", {"start": v(3.91, 9.31) * mm, "end": v(3.8, 9.31) * mm});
            skLineSegment(sketch, "E297", {"start": v(3.8, 9.31) * mm, "end": v(3.69, 9.31) * mm});
            skLineSegment(sketch, "E298", {"start": v(3.69, 9.31) * mm, "end": v(3.57, 9.31) * mm});
            skLineSegment(sketch, "E299", {"start": v(3.57, 9.31) * mm, "end": v(3.46, 9.31) * mm});
            skLineSegment(sketch, "E300", {"start": v(3.46, 9.31) * mm, "end": v(3.35, 9.31) * mm});
            skLineSegment(sketch, "E301", {"start": v(3.35, 9.31) * mm, "end": v(3.23, 9.31) * mm});
            skLineSegment(sketch, "E302", {"start": v(3.23, 9.31) * mm, "end": v(3.12, 9.31) * mm});
            skLineSegment(sketch, "E303", {"start": v(3.12, 9.31) * mm, "end": v(3, 9.31) * mm});
            skLineSegment(sketch, "E304", {"start": v(3, 9.31) * mm, "end": v(2.9, 9.31) * mm});
            skLineSegment(sketch, "E305", {"start": v(2.9, 9.31) * mm, "end": v(2.78, 9.31) * mm});
            skLineSegment(sketch, "E306", {"start": v(2.78, 9.31) * mm, "end": v(2.67, 9.31) * mm});
            skLineSegment(sketch, "E307", {"start": v(2.67, 9.31) * mm, "end": v(2.55, 9.31) * mm});
            skLineSegment(sketch, "E308", {"start": v(2.55, 9.31) * mm, "end": v(2.44, 9.31) * mm});
            skLineSegment(sketch, "E309", {"start": v(2.44, 9.31) * mm, "end": v(2.33, 9.31) * mm});
            skLineSegment(sketch, "E310", {"start": v(2.33, 9.31) * mm, "end": v(2.2, 9.3) * mm});
            skLineSegment(sketch, "E311", {"start": v(2.2, 9.3) * mm, "end": v(2.07, 9.28) * mm});
            skLineSegment(sketch, "E312", {"start": v(2.07, 9.28) * mm, "end": v(1.94, 9.25) * mm});
            skLineSegment(sketch, "E313", {"start": v(1.94, 9.25) * mm, "end": v(1.82, 9.2) * mm});
            skLineSegment(sketch, "E314", {"start": v(1.82, 9.2) * mm, "end": v(1.71, 9.15) * mm});
            skLineSegment(sketch, "E315", {"start": v(1.71, 9.15) * mm, "end": v(1.6, 9.09) * mm});
            skLineSegment(sketch, "E316", {"start": v(1.6, 9.09) * mm, "end": v(1.5, 9.02) * mm});
            skLineSegment(sketch, "E317", {"start": v(1.5, 9.02) * mm, "end": v(1.41, 8.93) * mm});
            skLineSegment(sketch, "E318", {"start": v(1.41, 8.93) * mm, "end": v(1.33, 8.84) * mm});
            skLineSegment(sketch, "E319", {"start": v(1.33, 8.84) * mm, "end": v(1.26, 8.74) * mm});
            skLineSegment(sketch, "E320", {"start": v(1.26, 8.74) * mm, "end": v(1.2, 8.63) * mm});
            skLineSegment(sketch, "E321", {"start": v(1.2, 8.63) * mm, "end": v(1.14, 8.52) * mm});
            skLineSegment(sketch, "E322", {"start": v(1.14, 8.52) * mm, "end": v(1.1, 8.4) * mm});
            skLineSegment(sketch, "E323", {"start": v(1.1, 8.4) * mm, "end": v(1.06, 8.28) * mm});
            skLineSegment(sketch, "E324", {"start": v(1.06, 8.28) * mm, "end": v(1.04, 8.15) * mm});
            skLineSegment(sketch, "E325", {"start": v(1.04, 8.15) * mm, "end": v(1.03, 8.02) * mm});
            skLineSegment(sketch, "E326", {"start": v(1.03, 8.02) * mm, "end": v(1.03, 7.9) * mm});
            skLineSegment(sketch, "E327", {"start": v(1.03, 7.9) * mm, "end": v(1.03, 7.8) * mm});
            skLineSegment(sketch, "E328", {"start": v(1.03, 7.8) * mm, "end": v(1.03, 7.68) * mm});
            skLineSegment(sketch, "E329", {"start": v(1.03, 7.68) * mm, "end": v(1.03, 7.56) * mm});
            skLineSegment(sketch, "E330", {"start": v(1.03, 7.56) * mm, "end": v(1.03, 7.45) * mm});
            skLineSegment(sketch, "E331", {"start": v(1.03, 7.45) * mm, "end": v(1.03, 7.34) * mm});
            skLineSegment(sketch, "E332", {"start": v(1.03, 7.34) * mm, "end": v(1.03, 7.23) * mm});
            skLineSegment(sketch, "E333", {"start": v(1.03, 7.23) * mm, "end": v(1.03, 7.11) * mm});
            skLineSegment(sketch, "E334", {"start": v(1.03, 7.11) * mm, "end": v(1.03, 7) * mm});
            skLineSegment(sketch, "E335", {"start": v(1.03, 7) * mm, "end": v(1.03, 6.89) * mm});
            skLineSegment(sketch, "E336", {"start": v(1.03, 6.89) * mm, "end": v(1.03, 6.77) * mm});
            skLineSegment(sketch, "E337", {"start": v(1.03, 6.77) * mm, "end": v(1.03, 6.66) * mm});
            skLineSegment(sketch, "E338", {"start": v(1.03, 6.66) * mm, "end": v(1.03, 6.55) * mm});
            skLineSegment(sketch, "E339", {"start": v(1.03, 6.55) * mm, "end": v(1.03, 6.43) * mm});
            skLineSegment(sketch, "E340", {"start": v(1.03, 6.43) * mm, "end": v(1.03, 6.32) * mm});
            skLineSegment(sketch, "E341", {"start": v(1.03, 6.32) * mm, "end": v(1.03, 6.2) * mm});
            skLineSegment(sketch, "E342", {"start": v(1.03, 6.2) * mm, "end": v(0.97, 6.2) * mm});
            skLineSegment(sketch, "E343", {"start": v(0.97, 6.2) * mm, "end": v(0.9, 6.2) * mm});
            skLineSegment(sketch, "E344", {"start": v(0.9, 6.2) * mm, "end": v(0.84, 6.2) * mm});
            skLineSegment(sketch, "E345", {"start": v(0.84, 6.2) * mm, "end": v(0.78, 6.2) * mm});
            skLineSegment(sketch, "E346", {"start": v(0.78, 6.2) * mm, "end": v(0.71, 6.2) * mm});
            skLineSegment(sketch, "E347", {"start": v(0.71, 6.2) * mm, "end": v(0.65, 6.2) * mm});
            skLineSegment(sketch, "E348", {"start": v(0.65, 6.2) * mm, "end": v(0.58, 6.2) * mm});
            skLineSegment(sketch, "E349", {"start": v(0.58, 6.2) * mm, "end": v(0.52, 6.2) * mm});
            skLineSegment(sketch, "E350", {"start": v(0.52, 6.2) * mm, "end": v(0.45, 6.2) * mm});
            skLineSegment(sketch, "E351", {"start": v(0.45, 6.2) * mm, "end": v(0.39, 6.2) * mm});
            skLineSegment(sketch, "E352", {"start": v(0.39, 6.2) * mm, "end": v(0.32, 6.2) * mm});
            skLineSegment(sketch, "E353", {"start": v(0.32, 6.2) * mm, "end": v(0.26, 6.2) * mm});
            skLineSegment(sketch, "E354", {"start": v(0.26, 6.2) * mm, "end": v(0.2, 6.2) * mm});
            skLineSegment(sketch, "E355", {"start": v(0.2, 6.2) * mm, "end": v(0.13, 6.2) * mm});
            skLineSegment(sketch, "E356", {"start": v(0.13, 6.2) * mm, "end": v(0.06, 6.2) * mm});
            skLineSegment(sketch, "E357", {"start": v(0.06, 6.2) * mm, "end": v(0, 6.2) * mm});
            skLineSegment(sketch, "E358", {"start": v(0, 6.2) * mm, "end": v(-0.06, 6.2) * mm});
            skLineSegment(sketch, "E359", {"start": v(-0.06, 6.2) * mm, "end": v(-0.13, 6.2) * mm});
            skLineSegment(sketch, "E360", {"start": v(-0.13, 6.2) * mm, "end": v(-0.2, 6.2) * mm});
            skLineSegment(sketch, "E361", {"start": v(-0.2, 6.2) * mm, "end": v(-0.26, 6.2) * mm});
            skLineSegment(sketch, "E362", {"start": v(-0.26, 6.2) * mm, "end": v(-0.32, 6.2) * mm});
            skLineSegment(sketch, "E363", {"start": v(-0.32, 6.2) * mm, "end": v(-0.39, 6.2) * mm});
            skLineSegment(sketch, "E364", {"start": v(-0.39, 6.2) * mm, "end": v(-0.45, 6.2) * mm});
            skLineSegment(sketch, "E365", {"start": v(-0.45, 6.2) * mm, "end": v(-0.52, 6.2) * mm});
            skLineSegment(sketch, "E366", {"start": v(-0.52, 6.2) * mm, "end": v(-0.58, 6.2) * mm});
            skLineSegment(sketch, "E367", {"start": v(-0.58, 6.2) * mm, "end": v(-0.65, 6.2) * mm});
            skLineSegment(sketch, "E368", {"start": v(-0.65, 6.2) * mm, "end": v(-0.71, 6.2) * mm});
            skLineSegment(sketch, "E369", {"start": v(-0.71, 6.2) * mm, "end": v(-0.78, 6.2) * mm});
            skLineSegment(sketch, "E370", {"start": v(-0.78, 6.2) * mm, "end": v(-0.84, 6.2) * mm});
            skLineSegment(sketch, "E371", {"start": v(-0.84, 6.2) * mm, "end": v(-0.9, 6.2) * mm});
            skLineSegment(sketch, "E372", {"start": v(-0.9, 6.2) * mm, "end": v(-0.97, 6.2) * mm});
            skLineSegment(sketch, "E373", {"start": v(-0.97, 6.2) * mm, "end": v(-1.03, 6.2) * mm});
            skLineSegment(sketch, "E374", {"start": v(-1.03, 6.2) * mm, "end": v(-1.03, 6.32) * mm});
            skLineSegment(sketch, "E375", {"start": v(-1.03, 6.32) * mm, "end": v(-1.03, 6.43) * mm});
            skLineSegment(sketch, "E376", {"start": v(-1.03, 6.43) * mm, "end": v(-1.03, 6.55) * mm});
            skLineSegment(sketch, "E377", {"start": v(-1.03, 6.55) * mm, "end": v(-1.03, 6.66) * mm});
            skLineSegment(sketch, "E378", {"start": v(-1.03, 6.66) * mm, "end": v(-1.03, 6.77) * mm});
            skLineSegment(sketch, "E379", {"start": v(-1.03, 6.77) * mm, "end": v(-1.03, 6.89) * mm});
            skLineSegment(sketch, "E380", {"start": v(-1.03, 6.89) * mm, "end": v(-1.03, 7) * mm});
            skLineSegment(sketch, "E381", {"start": v(-1.03, 7) * mm, "end": v(-1.03, 7.11) * mm});
            skLineSegment(sketch, "E382", {"start": v(-1.03, 7.11) * mm, "end": v(-1.03, 7.23) * mm});
            skLineSegment(sketch, "E383", {"start": v(-1.03, 7.23) * mm, "end": v(-1.03, 7.34) * mm});
            skLineSegment(sketch, "E384", {"start": v(-1.03, 7.34) * mm, "end": v(-1.03, 7.45) * mm});
            skLineSegment(sketch, "E385", {"start": v(-1.03, 7.45) * mm, "end": v(-1.03, 7.56) * mm});
            skLineSegment(sketch, "E386", {"start": v(-1.03, 7.56) * mm, "end": v(-1.03, 7.68) * mm});
            skLineSegment(sketch, "E387", {"start": v(-1.03, 7.68) * mm, "end": v(-1.03, 7.8) * mm});
            skLineSegment(sketch, "E388", {"start": v(-1.03, 7.8) * mm, "end": v(-1.03, 7.9) * mm});
            skLineSegment(sketch, "E389", {"start": v(-1.03, 7.9) * mm, "end": v(-1.03, 8.02) * mm});
            skLineSegment(sketch, "E390", {"start": v(-1.03, 8.02) * mm, "end": v(-1.04, 8.15) * mm});
            skLineSegment(sketch, "E391", {"start": v(-1.04, 8.15) * mm, "end": v(-1.06, 8.28) * mm});
            skLineSegment(sketch, "E392", {"start": v(-1.06, 8.28) * mm, "end": v(-1.1, 8.4) * mm});
            skLineSegment(sketch, "E393", {"start": v(-1.1, 8.4) * mm, "end": v(-1.14, 8.52) * mm});
            skLineSegment(sketch, "E394", {"start": v(-1.14, 8.52) * mm, "end": v(-1.2, 8.63) * mm});
            skLineSegment(sketch, "E395", {"start": v(-1.2, 8.63) * mm, "end": v(-1.26, 8.74) * mm});
            skLineSegment(sketch, "E396", {"start": v(-1.26, 8.74) * mm, "end": v(-1.33, 8.84) * mm});
            skLineSegment(sketch, "E397", {"start": v(-1.33, 8.84) * mm, "end": v(-1.41, 8.93) * mm});
            skLineSegment(sketch, "E398", {"start": v(-1.41, 8.93) * mm, "end": v(-1.5, 9.02) * mm});
            skLineSegment(sketch, "E399", {"start": v(-1.5, 9.02) * mm, "end": v(-1.6, 9.09) * mm});
            skLineSegment(sketch, "E400", {"start": v(-1.6, 9.09) * mm, "end": v(-1.71, 9.15) * mm});
            skLineSegment(sketch, "E401", {"start": v(-1.71, 9.15) * mm, "end": v(-1.82, 9.2) * mm});
            skLineSegment(sketch, "E402", {"start": v(-1.82, 9.2) * mm, "end": v(-1.94, 9.25) * mm});
            skLineSegment(sketch, "E403", {"start": v(-1.94, 9.25) * mm, "end": v(-2.07, 9.28) * mm});
            skLineSegment(sketch, "E404", {"start": v(-2.07, 9.28) * mm, "end": v(-2.2, 9.3) * mm});
            skLineSegment(sketch, "E405", {"start": v(-2.2, 9.3) * mm, "end": v(-2.33, 9.31) * mm});
            skLineSegment(sketch, "E406", {"start": v(-2.33, 9.31) * mm, "end": v(-2.44, 9.31) * mm});
            skLineSegment(sketch, "E407", {"start": v(-2.44, 9.31) * mm, "end": v(-2.55, 9.31) * mm});
            skLineSegment(sketch, "E408", {"start": v(-2.55, 9.31) * mm, "end": v(-2.67, 9.31) * mm});
            skLineSegment(sketch, "E409", {"start": v(-2.67, 9.31) * mm, "end": v(-2.78, 9.31) * mm});
            skLineSegment(sketch, "E410", {"start": v(-2.78, 9.31) * mm, "end": v(-2.9, 9.31) * mm});
            skLineSegment(sketch, "E411", {"start": v(-2.9, 9.31) * mm, "end": v(-3, 9.31) * mm});
            skLineSegment(sketch, "E412", {"start": v(-3, 9.31) * mm, "end": v(-3.12, 9.31) * mm});
            skLineSegment(sketch, "E413", {"start": v(-3.12, 9.31) * mm, "end": v(-3.23, 9.31) * mm});
            skLineSegment(sketch, "E414", {"start": v(-3.23, 9.31) * mm, "end": v(-3.35, 9.31) * mm});
            skLineSegment(sketch, "E415", {"start": v(-3.35, 9.31) * mm, "end": v(-3.46, 9.31) * mm});
            skLineSegment(sketch, "E416", {"start": v(-3.46, 9.31) * mm, "end": v(-3.57, 9.31) * mm});
            skLineSegment(sketch, "E417", {"start": v(-3.57, 9.31) * mm, "end": v(-3.69, 9.31) * mm});
            skLineSegment(sketch, "E418", {"start": v(-3.69, 9.31) * mm, "end": v(-3.8, 9.31) * mm});
            skLineSegment(sketch, "E419", {"start": v(-3.8, 9.31) * mm, "end": v(-3.91, 9.31) * mm});
            skLineSegment(sketch, "E420", {"start": v(-3.91, 9.31) * mm, "end": v(-4.02, 9.31) * mm});
            skLineSegment(sketch, "E421", {"start": v(-4.02, 9.31) * mm, "end": v(-4.14, 9.31) * mm});
            skLineSegment(sketch, "E422", {"start": v(-4.14, 9.31) * mm, "end": v(-4.14, 9.44) * mm});
            skLineSegment(sketch, "E423", {"start": v(-4.14, 9.44) * mm, "end": v(-4.14, 9.57) * mm});
            skLineSegment(sketch, "E424", {"start": v(-4.14, 9.57) * mm, "end": v(-4.14, 9.7) * mm});
            skLineSegment(sketch, "E425", {"start": v(-4.14, 9.7) * mm, "end": v(-4.14, 9.83) * mm});
            skLineSegment(sketch, "E426", {"start": v(-4.14, 9.83) * mm, "end": v(-4.14, 9.96) * mm});
            skLineSegment(sketch, "E427", {"start": v(-4.14, 9.96) * mm, "end": v(-4.14, 10.09) * mm});
            skLineSegment(sketch, "E428", {"start": v(-4.14, 10.09) * mm, "end": v(-4.14, 10.22) * mm});
            skLineSegment(sketch, "E429", {"start": v(-4.14, 10.22) * mm, "end": v(-4.14, 10.34) * mm});
            skLineSegment(sketch, "E430", {"start": v(-4.14, 10.34) * mm, "end": v(-4.14, 10.47) * mm});
            skLineSegment(sketch, "E431", {"start": v(-4.14, 10.47) * mm, "end": v(-4.14, 10.6) * mm});
            skLineSegment(sketch, "E432", {"start": v(-4.14, 10.6) * mm, "end": v(-4.14, 10.73) * mm});
            skLineSegment(sketch, "E433", {"start": v(-4.14, 10.73) * mm, "end": v(-4.14, 10.86) * mm});
            skLineSegment(sketch, "E434", {"start": v(-4.14, 10.86) * mm, "end": v(-4.14, 11) * mm});
            skLineSegment(sketch, "E435", {"start": v(-4.14, 11) * mm, "end": v(-4.14, 11.12) * mm});
            skLineSegment(sketch, "E436", {"start": v(-4.14, 11.12) * mm, "end": v(-4.14, 11.25) * mm});
            skLineSegment(sketch, "E437", {"start": v(-4.14, 11.25) * mm, "end": v(-4.14, 11.38) * mm});
            skLineSegment(sketch, "E438", {"start": v(-4.14, 11.38) * mm, "end": v(-4.14, 11.6) * mm});
            skLineSegment(sketch, "E439", {"start": v(-4.14, 11.6) * mm, "end": v(-4.14, 11.83) * mm});
            skLineSegment(sketch, "E440", {"start": v(-4.14, 11.83) * mm, "end": v(-4.14, 12.06) * mm});
            skLineSegment(sketch, "E441", {"start": v(-4.14, 12.06) * mm, "end": v(-4.14, 12.28) * mm});
            skLineSegment(sketch, "E442", {"start": v(-4.14, 12.28) * mm, "end": v(-4.14, 12.51) * mm});
            skLineSegment(sketch, "E443", {"start": v(-4.14, 12.51) * mm, "end": v(-4.14, 12.74) * mm});
            skLineSegment(sketch, "E444", {"start": v(-4.14, 12.74) * mm, "end": v(-4.14, 12.96) * mm});
            skLineSegment(sketch, "E445", {"start": v(-4.14, 12.96) * mm, "end": v(-4.14, 13.19) * mm});
            skLineSegment(sketch, "E446", {"start": v(-4.14, 13.19) * mm, "end": v(-4.14, 13.42) * mm});
            skLineSegment(sketch, "E447", {"start": v(-4.14, 13.42) * mm, "end": v(-4.14, 13.64) * mm});
            skLineSegment(sketch, "E448", {"start": v(-4.14, 13.64) * mm, "end": v(-4.14, 13.87) * mm});
            skLineSegment(sketch, "E449", {"start": v(-4.14, 13.87) * mm, "end": v(-4.14, 14.1) * mm});
            skLineSegment(sketch, "E450", {"start": v(-4.14, 14.1) * mm, "end": v(-4.14, 14.32) * mm});
            skLineSegment(sketch, "E451", {"start": v(-4.14, 14.32) * mm, "end": v(-4.14, 14.55) * mm});
            skLineSegment(sketch, "E452", {"start": v(-4.14, 14.55) * mm, "end": v(-4.14, 14.77) * mm});
            skLineSegment(sketch, "E453", {"start": v(-4.14, 14.77) * mm, "end": v(-4.14, 15) * mm});
            skLineSegment(sketch, "E454", {"start": v(-4.14, 15) * mm, "end": v(-4.27, 14.95) * mm});
            skLineSegment(sketch, "E455", {"start": v(-4.27, 14.95) * mm, "end": v(-4.4, 14.9) * mm});
            skLineSegment(sketch, "E456", {"start": v(-4.4, 14.9) * mm, "end": v(-4.53, 14.84) * mm});
            skLineSegment(sketch, "E457", {"start": v(-4.53, 14.84) * mm, "end": v(-4.66, 14.8) * mm});
            skLineSegment(sketch, "E458", {"start": v(-4.66, 14.8) * mm, "end": v(-4.78, 14.74) * mm});
            skLineSegment(sketch, "E459", {"start": v(-4.78, 14.74) * mm, "end": v(-4.91, 14.69) * mm});
            skLineSegment(sketch, "E460", {"start": v(-4.91, 14.69) * mm, "end": v(-5.04, 14.64) * mm});
            skLineSegment(sketch, "E461", {"start": v(-5.04, 14.64) * mm, "end": v(-5.17, 14.59) * mm});
            skLineSegment(sketch, "E462", {"start": v(-5.17, 14.59) * mm, "end": v(-5.3, 14.53) * mm});
            skLineSegment(sketch, "E463", {"start": v(-5.3, 14.53) * mm, "end": v(-5.43, 14.48) * mm});
            skLineSegment(sketch, "E464", {"start": v(-5.43, 14.48) * mm, "end": v(-5.56, 14.43) * mm});
            skLineSegment(sketch, "E465", {"start": v(-5.56, 14.43) * mm, "end": v(-5.69, 14.38) * mm});
            skLineSegment(sketch, "E466", {"start": v(-5.69, 14.38) * mm, "end": v(-5.82, 14.33) * mm});
            skLineSegment(sketch, "E467", {"start": v(-5.82, 14.33) * mm, "end": v(-5.95, 14.28) * mm});
            skLineSegment(sketch, "E468", {"start": v(-5.95, 14.28) * mm, "end": v(-6.08, 14.22) * mm});
            skLineSegment(sketch, "E469", {"start": v(-6.08, 14.22) * mm, "end": v(-6.2, 14.17) * mm});
            skLineSegment(sketch, "E470", {"start": v(-6.2, 14.17) * mm, "end": v(-6.24, 14.16) * mm});
            skLineSegment(sketch, "E471", {"start": v(-6.24, 14.16) * mm, "end": v(-6.27, 14.15) * mm});
            skLineSegment(sketch, "E472", {"start": v(-6.27, 14.15) * mm, "end": v(-6.3, 14.13) * mm});
            skLineSegment(sketch, "E473", {"start": v(-6.3, 14.13) * mm, "end": v(-6.34, 14.12) * mm});
            skLineSegment(sketch, "E474", {"start": v(-6.34, 14.12) * mm, "end": v(-6.37, 14.1) * mm});
            skLineSegment(sketch, "E475", {"start": v(-6.37, 14.1) * mm, "end": v(-6.4, 14.1) * mm});
            skLineSegment(sketch, "E476", {"start": v(-6.4, 14.1) * mm, "end": v(-6.43, 14.08) * mm});
            skLineSegment(sketch, "E477", {"start": v(-6.43, 14.08) * mm, "end": v(-6.47, 14.07) * mm});
            skLineSegment(sketch, "E478", {"start": v(-6.47, 14.07) * mm, "end": v(-6.5, 14.06) * mm});
            skLineSegment(sketch, "E479", {"start": v(-6.5, 14.06) * mm, "end": v(-6.53, 14.04) * mm});
            skLineSegment(sketch, "E480", {"start": v(-6.53, 14.04) * mm, "end": v(-6.56, 14.03) * mm});
            skLineSegment(sketch, "E481", {"start": v(-6.56, 14.03) * mm, "end": v(-6.6, 14.02) * mm});
            skLineSegment(sketch, "E482", {"start": v(-6.6, 14.02) * mm, "end": v(-6.63, 14) * mm});
            skLineSegment(sketch, "E483", {"start": v(-6.63, 14) * mm, "end": v(-6.66, 14) * mm});
            skLineSegment(sketch, "E484", {"start": v(-6.66, 14) * mm, "end": v(-6.7, 13.98) * mm});
            skLineSegment(sketch, "E485", {"start": v(-6.7, 13.98) * mm, "end": v(-6.72, 13.97) * mm});
            skLineSegment(sketch, "E486", {"start": v(-6.72, 13.97) * mm, "end": v(-6.86, 13.65) * mm});
            skLineSegment(sketch, "E487", {"start": v(-6.86, 13.65) * mm, "end": v(-7, 13.33) * mm});
            skLineSegment(sketch, "E488", {"start": v(-7, 13.33) * mm, "end": v(-7.12, 13) * mm});
            skLineSegment(sketch, "E489", {"start": v(-7.12, 13) * mm, "end": v(-7.26, 12.69) * mm});
            skLineSegment(sketch, "E490", {"start": v(-7.26, 12.69) * mm, "end": v(-7.39, 12.37) * mm});
            skLineSegment(sketch, "E491", {"start": v(-7.39, 12.37) * mm, "end": v(-7.52, 12.05) * mm});
            skLineSegment(sketch, "E492", {"start": v(-7.52, 12.05) * mm, "end": v(-7.66, 11.73) * mm});
            skLineSegment(sketch, "E493", {"start": v(-7.66, 11.73) * mm, "end": v(-7.79, 11.4) * mm});
            skLineSegment(sketch, "E494", {"start": v(-7.79, 11.4) * mm, "end": v(-7.92, 11.1) * mm});
            skLineSegment(sketch, "E495", {"start": v(-7.92, 11.1) * mm, "end": v(-8.06, 10.77) * mm});
            skLineSegment(sketch, "E496", {"start": v(-8.06, 10.77) * mm, "end": v(-8.19, 10.45) * mm});
            skLineSegment(sketch, "E497", {"start": v(-8.19, 10.45) * mm, "end": v(-8.32, 10.13) * mm});
            skLineSegment(sketch, "E498", {"start": v(-8.32, 10.13) * mm, "end": v(-8.45, 9.81) * mm});
            skLineSegment(sketch, "E499", {"start": v(-8.45, 9.81) * mm, "end": v(-8.59, 9.5) * mm});
            skLineSegment(sketch, "E500", {"start": v(-8.59, 9.5) * mm, "end": v(-8.72, 9.17) * mm});
            skLineSegment(sketch, "E501", {"start": v(-8.72, 9.17) * mm, "end": v(-8.85, 8.85) * mm});
            skLineSegment(sketch, "E502", {"start": v(-8.85, 8.85) * mm, "end": v(-9.17, 8.72) * mm});
            skLineSegment(sketch, "E503", {"start": v(-9.17, 8.72) * mm, "end": v(-9.5, 8.59) * mm});
            skLineSegment(sketch, "E504", {"start": v(-9.5, 8.59) * mm, "end": v(-9.81, 8.45) * mm});
            skLineSegment(sketch, "E505", {"start": v(-9.81, 8.45) * mm, "end": v(-10.13, 8.32) * mm});
            skLineSegment(sketch, "E506", {"start": v(-10.13, 8.32) * mm, "end": v(-10.45, 8.19) * mm});
            skLineSegment(sketch, "E507", {"start": v(-10.45, 8.19) * mm, "end": v(-10.77, 8.06) * mm});
            skLineSegment(sketch, "E508", {"start": v(-10.77, 8.06) * mm, "end": v(-11.1, 7.92) * mm});
            skLineSegment(sketch, "E509", {"start": v(-11.1, 7.92) * mm, "end": v(-11.4, 7.79) * mm});
            skLineSegment(sketch, "E510", {"start": v(-11.4, 7.79) * mm, "end": v(-11.73, 7.66) * mm});
            skLineSegment(sketch, "E511", {"start": v(-11.73, 7.66) * mm, "end": v(-12.05, 7.52) * mm});
            skLineSegment(sketch, "E512", {"start": v(-12.05, 7.52) * mm, "end": v(-12.37, 7.39) * mm});
            skLineSegment(sketch, "E513", {"start": v(-12.37, 7.39) * mm, "end": v(-12.69, 7.26) * mm});
            skLineSegment(sketch, "E514", {"start": v(-12.69, 7.26) * mm, "end": v(-13, 7.12) * mm});
            skLineSegment(sketch, "E515", {"start": v(-13, 7.12) * mm, "end": v(-13.33, 7) * mm});
            skLineSegment(sketch, "E516", {"start": v(-13.33, 7) * mm, "end": v(-13.65, 6.86) * mm});
            skLineSegment(sketch, "E517", {"start": v(-13.65, 6.86) * mm, "end": v(-13.97, 6.72) * mm});
            skLineSegment(sketch, "E518", {"start": v(-13.97, 6.72) * mm, "end": v(-13.98, 6.7) * mm});
            skLineSegment(sketch, "E519", {"start": v(-13.98, 6.7) * mm, "end": v(-14, 6.66) * mm});
            skLineSegment(sketch, "E520", {"start": v(-14, 6.66) * mm, "end": v(-14, 6.63) * mm});
            skLineSegment(sketch, "E521", {"start": v(-14, 6.63) * mm, "end": v(-14.02, 6.6) * mm});
            skLineSegment(sketch, "E522", {"start": v(-14.02, 6.6) * mm, "end": v(-14.03, 6.56) * mm});
            skLineSegment(sketch, "E523", {"start": v(-14.03, 6.56) * mm, "end": v(-14.04, 6.53) * mm});
            skLineSegment(sketch, "E524", {"start": v(-14.04, 6.53) * mm, "end": v(-14.06, 6.5) * mm});
            skLineSegment(sketch, "E525", {"start": v(-14.06, 6.5) * mm, "end": v(-14.07, 6.47) * mm});
            skLineSegment(sketch, "E526", {"start": v(-14.07, 6.47) * mm, "end": v(-14.08, 6.43) * mm});
            skLineSegment(sketch, "E527", {"start": v(-14.08, 6.43) * mm, "end": v(-14.1, 6.4) * mm});
            skLineSegment(sketch, "E528", {"start": v(-14.1, 6.4) * mm, "end": v(-14.1, 6.37) * mm});
            skLineSegment(sketch, "E529", {"start": v(-14.1, 6.37) * mm, "end": v(-14.12, 6.34) * mm});
            skLineSegment(sketch, "E530", {"start": v(-14.12, 6.34) * mm, "end": v(-14.13, 6.3) * mm});
            skLineSegment(sketch, "E531", {"start": v(-14.13, 6.3) * mm, "end": v(-14.15, 6.27) * mm});
            skLineSegment(sketch, "E532", {"start": v(-14.15, 6.27) * mm, "end": v(-14.16, 6.24) * mm});
            skLineSegment(sketch, "E533", {"start": v(-14.16, 6.24) * mm, "end": v(-14.17, 6.2) * mm});
            skLineSegment(sketch, "E534", {"start": v(-14.17, 6.2) * mm, "end": v(-14.22, 6.08) * mm});
            skLineSegment(sketch, "E535", {"start": v(-14.22, 6.08) * mm, "end": v(-14.28, 5.95) * mm});
            skLineSegment(sketch, "E536", {"start": v(-14.28, 5.95) * mm, "end": v(-14.33, 5.82) * mm});
            skLineSegment(sketch, "E537", {"start": v(-14.33, 5.82) * mm, "end": v(-14.38, 5.69) * mm});
            skLineSegment(sketch, "E538", {"start": v(-14.38, 5.69) * mm, "end": v(-14.43, 5.56) * mm});
            skLineSegment(sketch, "E539", {"start": v(-14.43, 5.56) * mm, "end": v(-14.48, 5.43) * mm});
            skLineSegment(sketch, "E540", {"start": v(-14.48, 5.43) * mm, "end": v(-14.53, 5.3) * mm});
            skLineSegment(sketch, "E541", {"start": v(-14.53, 5.3) * mm, "end": v(-14.59, 5.17) * mm});
            skLineSegment(sketch, "E542", {"start": v(-14.59, 5.17) * mm, "end": v(-14.64, 5.04) * mm});
            skLineSegment(sketch, "E543", {"start": v(-14.64, 5.04) * mm, "end": v(-14.69, 4.91) * mm});
            skLineSegment(sketch, "E544", {"start": v(-14.69, 4.91) * mm, "end": v(-14.74, 4.78) * mm});
            skLineSegment(sketch, "E545", {"start": v(-14.74, 4.78) * mm, "end": v(-14.8, 4.66) * mm});
            skLineSegment(sketch, "E546", {"start": v(-14.8, 4.66) * mm, "end": v(-14.84, 4.53) * mm});
            skLineSegment(sketch, "E547", {"start": v(-14.84, 4.53) * mm, "end": v(-14.9, 4.4) * mm});
            skLineSegment(sketch, "E548", {"start": v(-14.9, 4.4) * mm, "end": v(-14.95, 4.27) * mm});
            skLineSegment(sketch, "E549", {"start": v(-14.95, 4.27) * mm, "end": v(-15, 4.14) * mm});
            skLineSegment(sketch, "E550", {"start": v(-15, 4.14) * mm, "end": v(-14.77, 4.14) * mm});
            skLineSegment(sketch, "E551", {"start": v(-14.77, 4.14) * mm, "end": v(-14.55, 4.14) * mm});
            skLineSegment(sketch, "E552", {"start": v(-14.55, 4.14) * mm, "end": v(-14.32, 4.14) * mm});
            skLineSegment(sketch, "E553", {"start": v(-14.32, 4.14) * mm, "end": v(-14.1, 4.14) * mm});
            skLineSegment(sketch, "E554", {"start": v(-14.1, 4.14) * mm, "end": v(-13.87, 4.14) * mm});
            skLineSegment(sketch, "E555", {"start": v(-13.87, 4.14) * mm, "end": v(-13.64, 4.14) * mm});
            skLineSegment(sketch, "E556", {"start": v(-13.64, 4.14) * mm, "end": v(-13.42, 4.14) * mm});
            skLineSegment(sketch, "E557", {"start": v(-13.42, 4.14) * mm, "end": v(-13.19, 4.14) * mm});
            skLineSegment(sketch, "E558", {"start": v(-13.19, 4.14) * mm, "end": v(-12.96, 4.14) * mm});
            skLineSegment(sketch, "E559", {"start": v(-12.96, 4.14) * mm, "end": v(-12.74, 4.14) * mm});
            skLineSegment(sketch, "E560", {"start": v(-12.74, 4.14) * mm, "end": v(-12.51, 4.14) * mm});
            skLineSegment(sketch, "E561", {"start": v(-12.51, 4.14) * mm, "end": v(-12.28, 4.14) * mm});
            skLineSegment(sketch, "E562", {"start": v(-12.28, 4.14) * mm, "end": v(-12.06, 4.14) * mm});
            skLineSegment(sketch, "E563", {"start": v(-12.06, 4.14) * mm, "end": v(-11.83, 4.14) * mm});
            skLineSegment(sketch, "E564", {"start": v(-11.83, 4.14) * mm, "end": v(-11.6, 4.14) * mm});
            skLineSegment(sketch, "E565", {"start": v(-11.6, 4.14) * mm, "end": v(-11.38, 4.14) * mm});
            skLineSegment(sketch, "E566", {"start": v(-11.38, 4.14) * mm, "end": v(-11.25, 4.14) * mm});
            skLineSegment(sketch, "E567", {"start": v(-11.25, 4.14) * mm, "end": v(-11.12, 4.14) * mm});
            skLineSegment(sketch, "E568", {"start": v(-11.12, 4.14) * mm, "end": v(-11, 4.14) * mm});
            skLineSegment(sketch, "E569", {"start": v(-11, 4.14) * mm, "end": v(-10.86, 4.14) * mm});
            skLineSegment(sketch, "E570", {"start": v(-10.86, 4.14) * mm, "end": v(-10.73, 4.14) * mm});
            skLineSegment(sketch, "E571", {"start": v(-10.73, 4.14) * mm, "end": v(-10.6, 4.14) * mm});
            skLineSegment(sketch, "E572", {"start": v(-10.6, 4.14) * mm, "end": v(-10.47, 4.14) * mm});
            skLineSegment(sketch, "E573", {"start": v(-10.47, 4.14) * mm, "end": v(-10.34, 4.14) * mm});
            skLineSegment(sketch, "E574", {"start": v(-10.34, 4.14) * mm, "end": v(-10.22, 4.14) * mm});
            skLineSegment(sketch, "E575", {"start": v(-10.22, 4.14) * mm, "end": v(-10.09, 4.14) * mm});
            skLineSegment(sketch, "E576", {"start": v(-10.09, 4.14) * mm, "end": v(-9.96, 4.14) * mm});
            skLineSegment(sketch, "E577", {"start": v(-9.96, 4.14) * mm, "end": v(-9.83, 4.14) * mm});
            skLineSegment(sketch, "E578", {"start": v(-9.83, 4.14) * mm, "end": v(-9.7, 4.14) * mm});
            skLineSegment(sketch, "E579", {"start": v(-9.7, 4.14) * mm, "end": v(-9.57, 4.14) * mm});
            skLineSegment(sketch, "E580", {"start": v(-9.57, 4.14) * mm, "end": v(-9.44, 4.14) * mm});
            skLineSegment(sketch, "E581", {"start": v(-9.44, 4.14) * mm, "end": v(-9.31, 4.14) * mm});
            skLineSegment(sketch, "E582", {"start": v(-9.31, 4.14) * mm, "end": v(-9.31, 4.02) * mm});
            skLineSegment(sketch, "E583", {"start": v(-9.31, 4.02) * mm, "end": v(-9.31, 3.91) * mm});
            skLineSegment(sketch, "E584", {"start": v(-9.31, 3.91) * mm, "end": v(-9.31, 3.8) * mm});
            skLineSegment(sketch, "E585", {"start": v(-9.31, 3.8) * mm, "end": v(-9.31, 3.69) * mm});
            skLineSegment(sketch, "E586", {"start": v(-9.31, 3.69) * mm, "end": v(-9.31, 3.57) * mm});
            skLineSegment(sketch, "E587", {"start": v(-9.31, 3.57) * mm, "end": v(-9.31, 3.46) * mm});
            skLineSegment(sketch, "E588", {"start": v(-9.31, 3.46) * mm, "end": v(-9.31, 3.35) * mm});
            skLineSegment(sketch, "E589", {"start": v(-9.31, 3.35) * mm, "end": v(-9.31, 3.23) * mm});
            skLineSegment(sketch, "E590", {"start": v(-9.31, 3.23) * mm, "end": v(-9.31, 3.12) * mm});
            skLineSegment(sketch, "E591", {"start": v(-9.31, 3.12) * mm, "end": v(-9.31, 3) * mm});
            skLineSegment(sketch, "E592", {"start": v(-9.31, 3) * mm, "end": v(-9.31, 2.9) * mm});
            skLineSegment(sketch, "E593", {"start": v(-9.31, 2.9) * mm, "end": v(-9.31, 2.78) * mm});
            skLineSegment(sketch, "E594", {"start": v(-9.31, 2.78) * mm, "end": v(-9.31, 2.67) * mm});
            skLineSegment(sketch, "E595", {"start": v(-9.31, 2.67) * mm, "end": v(-9.31, 2.55) * mm});
            skLineSegment(sketch, "E596", {"start": v(-9.31, 2.55) * mm, "end": v(-9.31, 2.44) * mm});
            skLineSegment(sketch, "E597", {"start": v(-9.31, 2.44) * mm, "end": v(-9.31, 2.33) * mm});
            skLineSegment(sketch, "E598", {"start": v(-9.31, 2.33) * mm, "end": v(-9.3, 2.2) * mm});
            skLineSegment(sketch, "E599", {"start": v(-9.3, 2.2) * mm, "end": v(-9.28, 2.07) * mm});
            skLineSegment(sketch, "E600", {"start": v(-9.28, 2.07) * mm, "end": v(-9.25, 1.94) * mm});
            skLineSegment(sketch, "E601", {"start": v(-9.25, 1.94) * mm, "end": v(-9.2, 1.82) * mm});
            skLineSegment(sketch, "E602", {"start": v(-9.2, 1.82) * mm, "end": v(-9.15, 1.71) * mm});
            skLineSegment(sketch, "E603", {"start": v(-9.15, 1.71) * mm, "end": v(-9.09, 1.6) * mm});
            skLineSegment(sketch, "E604", {"start": v(-9.09, 1.6) * mm, "end": v(-9.02, 1.5) * mm});
            skLineSegment(sketch, "E605", {"start": v(-9.02, 1.5) * mm, "end": v(-8.93, 1.41) * mm});
            skLineSegment(sketch, "E606", {"start": v(-8.93, 1.41) * mm, "end": v(-8.84, 1.33) * mm});
            skLineSegment(sketch, "E607", {"start": v(-8.84, 1.33) * mm, "end": v(-8.74, 1.26) * mm});
            skLineSegment(sketch, "E608", {"start": v(-8.74, 1.26) * mm, "end": v(-8.63, 1.2) * mm});
            skLineSegment(sketch, "E609", {"start": v(-8.63, 1.2) * mm, "end": v(-8.52, 1.14) * mm});
            skLineSegment(sketch, "E610", {"start": v(-8.52, 1.14) * mm, "end": v(-8.4, 1.1) * mm});
            skLineSegment(sketch, "E611", {"start": v(-8.4, 1.1) * mm, "end": v(-8.28, 1.06) * mm});
            skLineSegment(sketch, "E612", {"start": v(-8.28, 1.06) * mm, "end": v(-8.15, 1.04) * mm});
            skLineSegment(sketch, "E613", {"start": v(-8.15, 1.04) * mm, "end": v(-8.02, 1.03) * mm});
            skLineSegment(sketch, "E614", {"start": v(-8.02, 1.03) * mm, "end": v(-7.9, 1.03) * mm});
            skLineSegment(sketch, "E615", {"start": v(-7.9, 1.03) * mm, "end": v(-7.8, 1.03) * mm});
            skLineSegment(sketch, "E616", {"start": v(-7.8, 1.03) * mm, "end": v(-7.68, 1.03) * mm});
            skLineSegment(sketch, "E617", {"start": v(-7.68, 1.03) * mm, "end": v(-7.56, 1.03) * mm});
            skLineSegment(sketch, "E618", {"start": v(-7.56, 1.03) * mm, "end": v(-7.45, 1.03) * mm});
            skLineSegment(sketch, "E619", {"start": v(-7.45, 1.03) * mm, "end": v(-7.34, 1.03) * mm});
            skLineSegment(sketch, "E620", {"start": v(-7.34, 1.03) * mm, "end": v(-7.23, 1.03) * mm});
            skLineSegment(sketch, "E621", {"start": v(-7.23, 1.03) * mm, "end": v(-7.11, 1.03) * mm});
            skLineSegment(sketch, "E622", {"start": v(-7.11, 1.03) * mm, "end": v(-7, 1.03) * mm});
            skLineSegment(sketch, "E623", {"start": v(-7, 1.03) * mm, "end": v(-6.89, 1.03) * mm});
            skLineSegment(sketch, "E624", {"start": v(-6.89, 1.03) * mm, "end": v(-6.77, 1.03) * mm});
            skLineSegment(sketch, "E625", {"start": v(-6.77, 1.03) * mm, "end": v(-6.66, 1.03) * mm});
            skLineSegment(sketch, "E626", {"start": v(-6.66, 1.03) * mm, "end": v(-6.55, 1.03) * mm});
            skLineSegment(sketch, "E627", {"start": v(-6.55, 1.03) * mm, "end": v(-6.43, 1.03) * mm});
            skLineSegment(sketch, "E628", {"start": v(-6.43, 1.03) * mm, "end": v(-6.32, 1.03) * mm});
            skLineSegment(sketch, "E629", {"start": v(-6.32, 1.03) * mm, "end": v(-6.2, 1.03) * mm});
            skLineSegment(sketch, "E630", {"start": v(-6.2, 1.03) * mm, "end": v(-6.2, 0.97) * mm});
            skLineSegment(sketch, "E631", {"start": v(-6.2, 0.97) * mm, "end": v(-6.2, 0.9) * mm});
            skLineSegment(sketch, "E632", {"start": v(-6.2, 0.9) * mm, "end": v(-6.2, 0.84) * mm});
            skLineSegment(sketch, "E633", {"start": v(-6.2, 0.84) * mm, "end": v(-6.2, 0.78) * mm});
            skLineSegment(sketch, "E634", {"start": v(-6.2, 0.78) * mm, "end": v(-6.2, 0.71) * mm});
            skLineSegment(sketch, "E635", {"start": v(-6.2, 0.71) * mm, "end": v(-6.2, 0.65) * mm});
            skLineSegment(sketch, "E636", {"start": v(-6.2, 0.65) * mm, "end": v(-6.2, 0.58) * mm});
            skLineSegment(sketch, "E637", {"start": v(-6.2, 0.58) * mm, "end": v(-6.2, 0.52) * mm});
            skLineSegment(sketch, "E638", {"start": v(-6.2, 0.52) * mm, "end": v(-6.2, 0.45) * mm});
            skLineSegment(sketch, "E639", {"start": v(-6.2, 0.45) * mm, "end": v(-6.2, 0.39) * mm});
            skLineSegment(sketch, "E640", {"start": v(-6.2, 0.39) * mm, "end": v(-6.2, 0.32) * mm});
            skLineSegment(sketch, "E641", {"start": v(-6.2, 0.32) * mm, "end": v(-6.2, 0.26) * mm});
            skLineSegment(sketch, "E642", {"start": v(-6.2, 0.26) * mm, "end": v(-6.2, 0.2) * mm});
            skLineSegment(sketch, "E643", {"start": v(-6.2, 0.2) * mm, "end": v(-6.2, 0.13) * mm});
            skLineSegment(sketch, "E644", {"start": v(-6.2, 0.13) * mm, "end": v(-6.2, 0.06) * mm});
            skLineSegment(sketch, "E645", {"start": v(-6.2, 0.06) * mm, "end": v(-6.2, 0) * mm});
            skLineSegment(sketch, "E646", {"start": v(-6.2, 0) * mm, "end": v(-6.2, -0.06) * mm});
            skLineSegment(sketch, "E647", {"start": v(-6.2, -0.06) * mm, "end": v(-6.2, -0.13) * mm});
            skLineSegment(sketch, "E648", {"start": v(-6.2, -0.13) * mm, "end": v(-6.2, -0.2) * mm});
            skLineSegment(sketch, "E649", {"start": v(-6.2, -0.2) * mm, "end": v(-6.2, -0.26) * mm});
            skLineSegment(sketch, "E650", {"start": v(-6.2, -0.26) * mm, "end": v(-6.2, -0.32) * mm});
            skLineSegment(sketch, "E651", {"start": v(-6.2, -0.32) * mm, "end": v(-6.2, -0.39) * mm});
            skLineSegment(sketch, "E652", {"start": v(-6.2, -0.39) * mm, "end": v(-6.2, -0.45) * mm});
            skLineSegment(sketch, "E653", {"start": v(-6.2, -0.45) * mm, "end": v(-6.2, -0.52) * mm});
            skLineSegment(sketch, "E654", {"start": v(-6.2, -0.52) * mm, "end": v(-6.2, -0.58) * mm});
            skLineSegment(sketch, "E655", {"start": v(-6.2, -0.58) * mm, "end": v(-6.2, -0.65) * mm});
            skLineSegment(sketch, "E656", {"start": v(-6.2, -0.65) * mm, "end": v(-6.2, -0.71) * mm});
            skLineSegment(sketch, "E657", {"start": v(-6.2, -0.71) * mm, "end": v(-6.2, -0.78) * mm});
            skLineSegment(sketch, "E658", {"start": v(-6.2, -0.78) * mm, "end": v(-6.2, -0.84) * mm});
            skLineSegment(sketch, "E659", {"start": v(-6.2, -0.84) * mm, "end": v(-6.2, -0.9) * mm});
            skLineSegment(sketch, "E660", {"start": v(-6.2, -0.9) * mm, "end": v(-6.2, -0.97) * mm});
            skLineSegment(sketch, "E661", {"start": v(-6.2, -0.97) * mm, "end": v(-6.2, -1.03) * mm});
            skLineSegment(sketch, "E662", {"start": v(-6.2, -1.03) * mm, "end": v(-6.32, -1.03) * mm});
            skLineSegment(sketch, "E663", {"start": v(-6.32, -1.03) * mm, "end": v(-6.43, -1.03) * mm});
            skLineSegment(sketch, "E664", {"start": v(-6.43, -1.03) * mm, "end": v(-6.55, -1.03) * mm});
            skLineSegment(sketch, "E665", {"start": v(-6.55, -1.03) * mm, "end": v(-6.66, -1.03) * mm});
            skLineSegment(sketch, "E666", {"start": v(-6.66, -1.03) * mm, "end": v(-6.77, -1.03) * mm});
            skLineSegment(sketch, "E667", {"start": v(-6.77, -1.03) * mm, "end": v(-6.89, -1.03) * mm});
            skLineSegment(sketch, "E668", {"start": v(-6.89, -1.03) * mm, "end": v(-7, -1.03) * mm});
            skLineSegment(sketch, "E669", {"start": v(-7, -1.03) * mm, "end": v(-7.11, -1.03) * mm});
            skLineSegment(sketch, "E670", {"start": v(-7.11, -1.03) * mm, "end": v(-7.23, -1.03) * mm});
            skLineSegment(sketch, "E671", {"start": v(-7.23, -1.03) * mm, "end": v(-7.34, -1.03) * mm});
            skLineSegment(sketch, "E672", {"start": v(-7.34, -1.03) * mm, "end": v(-7.45, -1.03) * mm});
            skLineSegment(sketch, "E673", {"start": v(-7.45, -1.03) * mm, "end": v(-7.56, -1.03) * mm});
            skLineSegment(sketch, "E674", {"start": v(-7.56, -1.03) * mm, "end": v(-7.68, -1.03) * mm});
            skLineSegment(sketch, "E675", {"start": v(-7.68, -1.03) * mm, "end": v(-7.8, -1.03) * mm});
            skLineSegment(sketch, "E676", {"start": v(-7.8, -1.03) * mm, "end": v(-7.9, -1.03) * mm});
            skLineSegment(sketch, "E677", {"start": v(-7.9, -1.03) * mm, "end": v(-8.02, -1.03) * mm});
            skLineSegment(sketch, "E678", {"start": v(-8.02, -1.03) * mm, "end": v(-8.15, -1.04) * mm});
            skLineSegment(sketch, "E679", {"start": v(-8.15, -1.04) * mm, "end": v(-8.28, -1.06) * mm});
            skLineSegment(sketch, "E680", {"start": v(-8.28, -1.06) * mm, "end": v(-8.4, -1.1) * mm});
            skLineSegment(sketch, "E681", {"start": v(-8.4, -1.1) * mm, "end": v(-8.52, -1.14) * mm});
            skLineSegment(sketch, "E682", {"start": v(-8.52, -1.14) * mm, "end": v(-8.63, -1.2) * mm});
            skLineSegment(sketch, "E683", {"start": v(-8.63, -1.2) * mm, "end": v(-8.74, -1.26) * mm});
            skLineSegment(sketch, "E684", {"start": v(-8.74, -1.26) * mm, "end": v(-8.84, -1.33) * mm});
            skLineSegment(sketch, "E685", {"start": v(-8.84, -1.33) * mm, "end": v(-8.93, -1.41) * mm});
            skLineSegment(sketch, "E686", {"start": v(-8.93, -1.41) * mm, "end": v(-9.02, -1.5) * mm});
            skLineSegment(sketch, "E687", {"start": v(-9.02, -1.5) * mm, "end": v(-9.09, -1.6) * mm});
            skLineSegment(sketch, "E688", {"start": v(-9.09, -1.6) * mm, "end": v(-9.15, -1.71) * mm});
            skLineSegment(sketch, "E689", {"start": v(-9.15, -1.71) * mm, "end": v(-9.2, -1.82) * mm});
            skLineSegment(sketch, "E690", {"start": v(-9.2, -1.82) * mm, "end": v(-9.25, -1.94) * mm});
            skLineSegment(sketch, "E691", {"start": v(-9.25, -1.94) * mm, "end": v(-9.28, -2.07) * mm});
            skLineSegment(sketch, "E692", {"start": v(-9.28, -2.07) * mm, "end": v(-9.3, -2.2) * mm});
            skLineSegment(sketch, "E693", {"start": v(-9.3, -2.2) * mm, "end": v(-9.31, -2.33) * mm});
            skLineSegment(sketch, "E694", {"start": v(-9.31, -2.33) * mm, "end": v(-9.31, -2.44) * mm});
            skLineSegment(sketch, "E695", {"start": v(-9.31, -2.44) * mm, "end": v(-9.31, -2.55) * mm});
            skLineSegment(sketch, "E696", {"start": v(-9.31, -2.55) * mm, "end": v(-9.31, -2.67) * mm});
            skLineSegment(sketch, "E697", {"start": v(-9.31, -2.67) * mm, "end": v(-9.31, -2.78) * mm});
            skLineSegment(sketch, "E698", {"start": v(-9.31, -2.78) * mm, "end": v(-9.31, -2.9) * mm});
            skLineSegment(sketch, "E699", {"start": v(-9.31, -2.9) * mm, "end": v(-9.31, -3) * mm});
            skLineSegment(sketch, "E700", {"start": v(-9.31, -3) * mm, "end": v(-9.31, -3.12) * mm});
            skLineSegment(sketch, "E701", {"start": v(-9.31, -3.12) * mm, "end": v(-9.31, -3.23) * mm});
            skLineSegment(sketch, "E702", {"start": v(-9.31, -3.23) * mm, "end": v(-9.31, -3.35) * mm});
            skLineSegment(sketch, "E703", {"start": v(-9.31, -3.35) * mm, "end": v(-9.31, -3.46) * mm});
            skLineSegment(sketch, "E704", {"start": v(-9.31, -3.46) * mm, "end": v(-9.31, -3.57) * mm});
            skLineSegment(sketch, "E705", {"start": v(-9.31, -3.57) * mm, "end": v(-9.31, -3.69) * mm});
            skLineSegment(sketch, "E706", {"start": v(-9.31, -3.69) * mm, "end": v(-9.31, -3.8) * mm});
            skLineSegment(sketch, "E707", {"start": v(-9.31, -3.8) * mm, "end": v(-9.31, -3.91) * mm});
            skLineSegment(sketch, "E708", {"start": v(-9.31, -3.91) * mm, "end": v(-9.31, -4.02) * mm});
            skLineSegment(sketch, "E709", {"start": v(-9.31, -4.02) * mm, "end": v(-9.31, -4.14) * mm});
            skLineSegment(sketch, "E710", {"start": v(-9.31, -4.14) * mm, "end": v(-9.44, -4.14) * mm});
            skLineSegment(sketch, "E711", {"start": v(-9.44, -4.14) * mm, "end": v(-9.57, -4.14) * mm});
            skLineSegment(sketch, "E712", {"start": v(-9.57, -4.14) * mm, "end": v(-9.7, -4.14) * mm});
            skLineSegment(sketch, "E713", {"start": v(-9.7, -4.14) * mm, "end": v(-9.83, -4.14) * mm});
            skLineSegment(sketch, "E714", {"start": v(-9.83, -4.14) * mm, "end": v(-9.96, -4.14) * mm});
            skLineSegment(sketch, "E715", {"start": v(-9.96, -4.14) * mm, "end": v(-10.09, -4.14) * mm});
            skLineSegment(sketch, "E716", {"start": v(-10.09, -4.14) * mm, "end": v(-10.22, -4.14) * mm});
            skLineSegment(sketch, "E717", {"start": v(-10.22, -4.14) * mm, "end": v(-10.34, -4.14) * mm});
            skLineSegment(sketch, "E718", {"start": v(-10.34, -4.14) * mm, "end": v(-10.47, -4.14) * mm});
            skLineSegment(sketch, "E719", {"start": v(-10.47, -4.14) * mm, "end": v(-10.6, -4.14) * mm});
            skLineSegment(sketch, "E720", {"start": v(-10.6, -4.14) * mm, "end": v(-10.73, -4.14) * mm});
            skLineSegment(sketch, "E721", {"start": v(-10.73, -4.14) * mm, "end": v(-10.86, -4.14) * mm});
            skLineSegment(sketch, "E722", {"start": v(-10.86, -4.14) * mm, "end": v(-11, -4.14) * mm});
            skLineSegment(sketch, "E723", {"start": v(-11, -4.14) * mm, "end": v(-11.12, -4.14) * mm});
            skLineSegment(sketch, "E724", {"start": v(-11.12, -4.14) * mm, "end": v(-11.25, -4.14) * mm});
            skLineSegment(sketch, "E725", {"start": v(-11.25, -4.14) * mm, "end": v(-11.38, -4.14) * mm});
            skLineSegment(sketch, "E726", {"start": v(-11.38, -4.14) * mm, "end": v(-11.6, -4.14) * mm});
            skLineSegment(sketch, "E727", {"start": v(-11.6, -4.14) * mm, "end": v(-11.83, -4.14) * mm});
            skLineSegment(sketch, "E728", {"start": v(-11.83, -4.14) * mm, "end": v(-12.06, -4.14) * mm});
            skLineSegment(sketch, "E729", {"start": v(-12.06, -4.14) * mm, "end": v(-12.28, -4.14) * mm});
            skLineSegment(sketch, "E730", {"start": v(-12.28, -4.14) * mm, "end": v(-12.51, -4.14) * mm});
            skLineSegment(sketch, "E731", {"start": v(-12.51, -4.14) * mm, "end": v(-12.74, -4.14) * mm});
            skLineSegment(sketch, "E732", {"start": v(-12.74, -4.14) * mm, "end": v(-12.96, -4.14) * mm});
            skLineSegment(sketch, "E733", {"start": v(-12.96, -4.14) * mm, "end": v(-13.19, -4.14) * mm});
            skLineSegment(sketch, "E734", {"start": v(-13.19, -4.14) * mm, "end": v(-13.42, -4.14) * mm});
            skLineSegment(sketch, "E735", {"start": v(-13.42, -4.14) * mm, "end": v(-13.64, -4.14) * mm});
            skLineSegment(sketch, "E736", {"start": v(-13.64, -4.14) * mm, "end": v(-13.87, -4.14) * mm});
            skLineSegment(sketch, "E737", {"start": v(-13.87, -4.14) * mm, "end": v(-14.1, -4.14) * mm});
            skLineSegment(sketch, "E738", {"start": v(-14.1, -4.14) * mm, "end": v(-14.32, -4.14) * mm});
            skLineSegment(sketch, "E739", {"start": v(-14.32, -4.14) * mm, "end": v(-14.55, -4.14) * mm});
            skLineSegment(sketch, "E740", {"start": v(-14.55, -4.14) * mm, "end": v(-14.77, -4.14) * mm});
            skLineSegment(sketch, "E741", {"start": v(-14.77, -4.14) * mm, "end": v(-15, -4.14) * mm});
            skLineSegment(sketch, "E742", {"start": v(-15, -4.14) * mm, "end": v(-14.95, -4.27) * mm});
            skLineSegment(sketch, "E743", {"start": v(-14.95, -4.27) * mm, "end": v(-14.9, -4.4) * mm});
            skLineSegment(sketch, "E744", {"start": v(-14.9, -4.4) * mm, "end": v(-14.84, -4.53) * mm});
            skLineSegment(sketch, "E745", {"start": v(-14.84, -4.53) * mm, "end": v(-14.8, -4.66) * mm});
            skLineSegment(sketch, "E746", {"start": v(-14.8, -4.66) * mm, "end": v(-14.74, -4.78) * mm});
            skLineSegment(sketch, "E747", {"start": v(-14.74, -4.78) * mm, "end": v(-14.69, -4.91) * mm});
            skLineSegment(sketch, "E748", {"start": v(-14.69, -4.91) * mm, "end": v(-14.64, -5.04) * mm});
            skLineSegment(sketch, "E749", {"start": v(-14.64, -5.04) * mm, "end": v(-14.59, -5.17) * mm});
            skLineSegment(sketch, "E750", {"start": v(-14.59, -5.17) * mm, "end": v(-14.53, -5.3) * mm});
            skLineSegment(sketch, "E751", {"start": v(-14.53, -5.3) * mm, "end": v(-14.48, -5.43) * mm});
            skLineSegment(sketch, "E752", {"start": v(-14.48, -5.43) * mm, "end": v(-14.43, -5.56) * mm});
            skLineSegment(sketch, "E753", {"start": v(-14.43, -5.56) * mm, "end": v(-14.38, -5.69) * mm});
            skLineSegment(sketch, "E754", {"start": v(-14.38, -5.69) * mm, "end": v(-14.33, -5.82) * mm});
            skLineSegment(sketch, "E755", {"start": v(-14.33, -5.82) * mm, "end": v(-14.28, -5.95) * mm});
            skLineSegment(sketch, "E756", {"start": v(-14.28, -5.95) * mm, "end": v(-14.22, -6.08) * mm});
            skLineSegment(sketch, "E757", {"start": v(-14.22, -6.08) * mm, "end": v(-14.17, -6.2) * mm});
            skLineSegment(sketch, "E758", {"start": v(-14.17, -6.2) * mm, "end": v(-14.16, -6.24) * mm});
            skLineSegment(sketch, "E759", {"start": v(-14.16, -6.24) * mm, "end": v(-14.15, -6.27) * mm});
            skLineSegment(sketch, "E760", {"start": v(-14.15, -6.27) * mm, "end": v(-14.13, -6.3) * mm});
            skLineSegment(sketch, "E761", {"start": v(-14.13, -6.3) * mm, "end": v(-14.12, -6.34) * mm});
            skLineSegment(sketch, "E762", {"start": v(-14.12, -6.34) * mm, "end": v(-14.1, -6.37) * mm});
            skLineSegment(sketch, "E763", {"start": v(-14.1, -6.37) * mm, "end": v(-14.1, -6.4) * mm});
            skLineSegment(sketch, "E764", {"start": v(-14.1, -6.4) * mm, "end": v(-14.08, -6.43) * mm});
            skLineSegment(sketch, "E765", {"start": v(-14.08, -6.43) * mm, "end": v(-14.07, -6.47) * mm});
            skLineSegment(sketch, "E766", {"start": v(-14.07, -6.47) * mm, "end": v(-14.06, -6.5) * mm});
            skLineSegment(sketch, "E767", {"start": v(-14.06, -6.5) * mm, "end": v(-14.04, -6.53) * mm});
            skLineSegment(sketch, "E768", {"start": v(-14.04, -6.53) * mm, "end": v(-14.03, -6.56) * mm});
            skLineSegment(sketch, "E769", {"start": v(-14.03, -6.56) * mm, "end": v(-14.02, -6.6) * mm});
            skLineSegment(sketch, "E770", {"start": v(-14.02, -6.6) * mm, "end": v(-14, -6.63) * mm});
            skLineSegment(sketch, "E771", {"start": v(-14, -6.63) * mm, "end": v(-14, -6.66) * mm});
            skLineSegment(sketch, "E772", {"start": v(-14, -6.66) * mm, "end": v(-13.98, -6.7) * mm});
            skLineSegment(sketch, "E773", {"start": v(-13.98, -6.7) * mm, "end": v(-13.97, -6.72) * mm});
            skLineSegment(sketch, "E774", {"start": v(-13.97, -6.72) * mm, "end": v(-13.65, -6.86) * mm});
            skLineSegment(sketch, "E775", {"start": v(-13.65, -6.86) * mm, "end": v(-13.33, -7) * mm});
            skLineSegment(sketch, "E776", {"start": v(-13.33, -7) * mm, "end": v(-13, -7.12) * mm});
            skLineSegment(sketch, "E777", {"start": v(-13, -7.12) * mm, "end": v(-12.69, -7.26) * mm});
            skLineSegment(sketch, "E778", {"start": v(-12.69, -7.26) * mm, "end": v(-12.37, -7.39) * mm});
            skLineSegment(sketch, "E779", {"start": v(-12.37, -7.39) * mm, "end": v(-12.05, -7.52) * mm});
            skLineSegment(sketch, "E780", {"start": v(-12.05, -7.52) * mm, "end": v(-11.73, -7.66) * mm});
            skLineSegment(sketch, "E781", {"start": v(-11.73, -7.66) * mm, "end": v(-11.4, -7.79) * mm});
            skLineSegment(sketch, "E782", {"start": v(-11.4, -7.79) * mm, "end": v(-11.1, -7.92) * mm});
            skLineSegment(sketch, "E783", {"start": v(-11.1, -7.92) * mm, "end": v(-10.77, -8.06) * mm});
            skLineSegment(sketch, "E784", {"start": v(-10.77, -8.06) * mm, "end": v(-10.45, -8.19) * mm});
            skLineSegment(sketch, "E785", {"start": v(-10.45, -8.19) * mm, "end": v(-10.13, -8.32) * mm});
            skLineSegment(sketch, "E786", {"start": v(-10.13, -8.32) * mm, "end": v(-9.81, -8.45) * mm});
            skLineSegment(sketch, "E787", {"start": v(-9.81, -8.45) * mm, "end": v(-9.5, -8.59) * mm});
            skLineSegment(sketch, "E788", {"start": v(-9.5, -8.59) * mm, "end": v(-9.17, -8.72) * mm});
            skLineSegment(sketch, "E789", {"start": v(-9.17, -8.72) * mm, "end": v(-8.85, -8.85) * mm});
            skLineSegment(sketch, "E790", {"start": v(-8.85, -8.85) * mm, "end": v(-8.72, -9.17) * mm});
            skLineSegment(sketch, "E791", {"start": v(-8.72, -9.17) * mm, "end": v(-8.59, -9.5) * mm});
            skLineSegment(sketch, "E792", {"start": v(-8.59, -9.5) * mm, "end": v(-8.45, -9.81) * mm});
            skLineSegment(sketch, "E793", {"start": v(-8.45, -9.81) * mm, "end": v(-8.32, -10.13) * mm});
            skLineSegment(sketch, "E794", {"start": v(-8.32, -10.13) * mm, "end": v(-8.19, -10.45) * mm});
            skLineSegment(sketch, "E795", {"start": v(-8.19, -10.45) * mm, "end": v(-8.06, -10.77) * mm});
            skLineSegment(sketch, "E796", {"start": v(-8.06, -10.77) * mm, "end": v(-7.92, -11.1) * mm});
            skLineSegment(sketch, "E797", {"start": v(-7.92, -11.1) * mm, "end": v(-7.79, -11.4) * mm});
            skLineSegment(sketch, "E798", {"start": v(-7.79, -11.4) * mm, "end": v(-7.66, -11.73) * mm});
            skLineSegment(sketch, "E799", {"start": v(-7.66, -11.73) * mm, "end": v(-7.52, -12.05) * mm});
            skLineSegment(sketch, "E800", {"start": v(-7.52, -12.05) * mm, "end": v(-7.39, -12.37) * mm});
            skLineSegment(sketch, "E801", {"start": v(-7.39, -12.37) * mm, "end": v(-7.26, -12.69) * mm});
            skLineSegment(sketch, "E802", {"start": v(-7.26, -12.69) * mm, "end": v(-7.12, -13) * mm});
            skLineSegment(sketch, "E803", {"start": v(-7.12, -13) * mm, "end": v(-7, -13.33) * mm});
            skLineSegment(sketch, "E804", {"start": v(-7, -13.33) * mm, "end": v(-6.86, -13.65) * mm});
            skLineSegment(sketch, "E805", {"start": v(-6.86, -13.65) * mm, "end": v(-6.72, -13.97) * mm});
            skLineSegment(sketch, "E806", {"start": v(-6.72, -13.97) * mm, "end": v(-6.7, -13.98) * mm});
            skLineSegment(sketch, "E807", {"start": v(-6.7, -13.98) * mm, "end": v(-6.66, -14) * mm});
            skLineSegment(sketch, "E808", {"start": v(-6.66, -14) * mm, "end": v(-6.63, -14) * mm});
            skLineSegment(sketch, "E809", {"start": v(-6.63, -14) * mm, "end": v(-6.6, -14.02) * mm});
            skLineSegment(sketch, "E810", {"start": v(-6.6, -14.02) * mm, "end": v(-6.56, -14.03) * mm});
            skLineSegment(sketch, "E811", {"start": v(-6.56, -14.03) * mm, "end": v(-6.53, -14.04) * mm});
            skLineSegment(sketch, "E812", {"start": v(-6.53, -14.04) * mm, "end": v(-6.5, -14.06) * mm});
            skLineSegment(sketch, "E813", {"start": v(-6.5, -14.06) * mm, "end": v(-6.47, -14.07) * mm});
            skLineSegment(sketch, "E814", {"start": v(-6.47, -14.07) * mm, "end": v(-6.43, -14.08) * mm});
            skLineSegment(sketch, "E815", {"start": v(-6.43, -14.08) * mm, "end": v(-6.4, -14.1) * mm});
            skLineSegment(sketch, "E816", {"start": v(-6.4, -14.1) * mm, "end": v(-6.37, -14.1) * mm});
            skLineSegment(sketch, "E817", {"start": v(-6.37, -14.1) * mm, "end": v(-6.34, -14.12) * mm});
            skLineSegment(sketch, "E818", {"start": v(-6.34, -14.12) * mm, "end": v(-6.3, -14.13) * mm});
            skLineSegment(sketch, "E819", {"start": v(-6.3, -14.13) * mm, "end": v(-6.27, -14.15) * mm});
            skLineSegment(sketch, "E820", {"start": v(-6.27, -14.15) * mm, "end": v(-6.24, -14.16) * mm});
            skLineSegment(sketch, "E821", {"start": v(-6.24, -14.16) * mm, "end": v(-6.2, -14.17) * mm});
            skLineSegment(sketch, "E822", {"start": v(-6.2, -14.17) * mm, "end": v(-6.08, -14.22) * mm});
            skLineSegment(sketch, "E823", {"start": v(-6.08, -14.22) * mm, "end": v(-5.95, -14.28) * mm});
            skLineSegment(sketch, "E824", {"start": v(-5.95, -14.28) * mm, "end": v(-5.82, -14.33) * mm});
            skLineSegment(sketch, "E825", {"start": v(-5.82, -14.33) * mm, "end": v(-5.69, -14.38) * mm});
            skLineSegment(sketch, "E826", {"start": v(-5.69, -14.38) * mm, "end": v(-5.56, -14.43) * mm});
            skLineSegment(sketch, "E827", {"start": v(-5.56, -14.43) * mm, "end": v(-5.43, -14.48) * mm});
            skLineSegment(sketch, "E828", {"start": v(-5.43, -14.48) * mm, "end": v(-5.3, -14.53) * mm});
            skLineSegment(sketch, "E829", {"start": v(-5.3, -14.53) * mm, "end": v(-5.17, -14.59) * mm});
            skLineSegment(sketch, "E830", {"start": v(-5.17, -14.59) * mm, "end": v(-5.04, -14.64) * mm});
            skLineSegment(sketch, "E831", {"start": v(-5.04, -14.64) * mm, "end": v(-4.91, -14.69) * mm});
            skLineSegment(sketch, "E832", {"start": v(-4.91, -14.69) * mm, "end": v(-4.78, -14.74) * mm});
            skLineSegment(sketch, "E833", {"start": v(-4.78, -14.74) * mm, "end": v(-4.66, -14.8) * mm});
            skLineSegment(sketch, "E834", {"start": v(-4.66, -14.8) * mm, "end": v(-4.53, -14.84) * mm});
            skLineSegment(sketch, "E835", {"start": v(-4.53, -14.84) * mm, "end": v(-4.4, -14.9) * mm});
            skLineSegment(sketch, "E836", {"start": v(-4.4, -14.9) * mm, "end": v(-4.27, -14.95) * mm});
            skLineSegment(sketch, "E837", {"start": v(-4.27, -14.95) * mm, "end": v(-4.14, -15) * mm});
            skLineSegment(sketch, "E838", {"start": v(-4.14, -15) * mm, "end": v(-4.14, -14.77) * mm});
            skLineSegment(sketch, "E839", {"start": v(-4.14, -14.77) * mm, "end": v(-4.14, -14.55) * mm});
            skLineSegment(sketch, "E840", {"start": v(-4.14, -14.55) * mm, "end": v(-4.14, -14.32) * mm});
            skLineSegment(sketch, "E841", {"start": v(-4.14, -14.32) * mm, "end": v(-4.14, -14.1) * mm});
            skLineSegment(sketch, "E842", {"start": v(-4.14, -14.1) * mm, "end": v(-4.14, -13.87) * mm});
            skLineSegment(sketch, "E843", {"start": v(-4.14, -13.87) * mm, "end": v(-4.14, -13.64) * mm});
            skLineSegment(sketch, "E844", {"start": v(-4.14, -13.64) * mm, "end": v(-4.14, -13.42) * mm});
            skLineSegment(sketch, "E845", {"start": v(-4.14, -13.42) * mm, "end": v(-4.14, -13.19) * mm});
            skLineSegment(sketch, "E846", {"start": v(-4.14, -13.19) * mm, "end": v(-4.14, -12.96) * mm});
            skLineSegment(sketch, "E847", {"start": v(-4.14, -12.96) * mm, "end": v(-4.14, -12.74) * mm});
            skLineSegment(sketch, "E848", {"start": v(-4.14, -12.74) * mm, "end": v(-4.14, -12.51) * mm});
            skLineSegment(sketch, "E849", {"start": v(-4.14, -12.51) * mm, "end": v(-4.14, -12.28) * mm});
            skLineSegment(sketch, "E850", {"start": v(-4.14, -12.28) * mm, "end": v(-4.14, -12.06) * mm});
            skLineSegment(sketch, "E851", {"start": v(-4.14, -12.06) * mm, "end": v(-4.14, -11.83) * mm});
            skLineSegment(sketch, "E852", {"start": v(-4.14, -11.83) * mm, "end": v(-4.14, -11.6) * mm});
            skLineSegment(sketch, "E853", {"start": v(-4.14, -11.6) * mm, "end": v(-4.14, -11.38) * mm});
            skLineSegment(sketch, "E854", {"start": v(-4.14, -11.38) * mm, "end": v(-4.14, -11.25) * mm});
            skLineSegment(sketch, "E855", {"start": v(-4.14, -11.25) * mm, "end": v(-4.14, -11.12) * mm});
            skLineSegment(sketch, "E856", {"start": v(-4.14, -11.12) * mm, "end": v(-4.14, -11) * mm});
            skLineSegment(sketch, "E857", {"start": v(-4.14, -11) * mm, "end": v(-4.14, -10.86) * mm});
            skLineSegment(sketch, "E858", {"start": v(-4.14, -10.86) * mm, "end": v(-4.14, -10.73) * mm});
            skLineSegment(sketch, "E859", {"start": v(-4.14, -10.73) * mm, "end": v(-4.14, -10.6) * mm});
            skLineSegment(sketch, "E860", {"start": v(-4.14, -10.6) * mm, "end": v(-4.14, -10.47) * mm});
            skLineSegment(sketch, "E861", {"start": v(-4.14, -10.47) * mm, "end": v(-4.14, -10.34) * mm});
            skLineSegment(sketch, "E862", {"start": v(-4.14, -10.34) * mm, "end": v(-4.14, -10.22) * mm});
            skLineSegment(sketch, "E863", {"start": v(-4.14, -10.22) * mm, "end": v(-4.14, -10.09) * mm});
            skLineSegment(sketch, "E864", {"start": v(-4.14, -10.09) * mm, "end": v(-4.14, -9.96) * mm});
            skLineSegment(sketch, "E865", {"start": v(-4.14, -9.96) * mm, "end": v(-4.14, -9.83) * mm});
            skLineSegment(sketch, "E866", {"start": v(-4.14, -9.83) * mm, "end": v(-4.14, -9.7) * mm});
            skLineSegment(sketch, "E867", {"start": v(-4.14, -9.7) * mm, "end": v(-4.14, -9.57) * mm});
            skLineSegment(sketch, "E868", {"start": v(-4.14, -9.57) * mm, "end": v(-4.14, -9.44) * mm});
            skLineSegment(sketch, "E869", {"start": v(-4.14, -9.44) * mm, "end": v(-4.14, -9.31) * mm});
            skLineSegment(sketch, "E870", {"start": v(-4.14, -9.31) * mm, "end": v(-4.02, -9.31) * mm});
            skLineSegment(sketch, "E871", {"start": v(-4.02, -9.31) * mm, "end": v(-3.91, -9.31) * mm});
            skLineSegment(sketch, "E872", {"start": v(-3.91, -9.31) * mm, "end": v(-3.8, -9.31) * mm});
            skLineSegment(sketch, "E873", {"start": v(-3.8, -9.31) * mm, "end": v(-3.69, -9.31) * mm});
            skLineSegment(sketch, "E874", {"start": v(-3.69, -9.31) * mm, "end": v(-3.57, -9.31) * mm});
            skLineSegment(sketch, "E875", {"start": v(-3.57, -9.31) * mm, "end": v(-3.46, -9.31) * mm});
            skLineSegment(sketch, "E876", {"start": v(-3.46, -9.31) * mm, "end": v(-3.35, -9.31) * mm});
            skLineSegment(sketch, "E877", {"start": v(-3.35, -9.31) * mm, "end": v(-3.23, -9.31) * mm});
            skLineSegment(sketch, "E878", {"start": v(-3.23, -9.31) * mm, "end": v(-3.12, -9.31) * mm});
            skLineSegment(sketch, "E879", {"start": v(-3.12, -9.31) * mm, "end": v(-3, -9.31) * mm});
            skLineSegment(sketch, "E880", {"start": v(-3, -9.31) * mm, "end": v(-2.9, -9.31) * mm});
            skLineSegment(sketch, "E881", {"start": v(-2.9, -9.31) * mm, "end": v(-2.78, -9.31) * mm});
            skLineSegment(sketch, "E882", {"start": v(-2.78, -9.31) * mm, "end": v(-2.67, -9.31) * mm});
            skLineSegment(sketch, "E883", {"start": v(-2.67, -9.31) * mm, "end": v(-2.55, -9.31) * mm});
            skLineSegment(sketch, "E884", {"start": v(-2.55, -9.31) * mm, "end": v(-2.44, -9.31) * mm});
            skLineSegment(sketch, "E885", {"start": v(-2.44, -9.31) * mm, "end": v(-2.33, -9.31) * mm});
            skLineSegment(sketch, "E886", {"start": v(-2.33, -9.31) * mm, "end": v(-2.2, -9.3) * mm});
            skLineSegment(sketch, "E887", {"start": v(-2.2, -9.3) * mm, "end": v(-2.07, -9.28) * mm});
            skLineSegment(sketch, "E888", {"start": v(-2.07, -9.28) * mm, "end": v(-1.94, -9.25) * mm});
            skLineSegment(sketch, "E889", {"start": v(-1.94, -9.25) * mm, "end": v(-1.82, -9.2) * mm});
            skLineSegment(sketch, "E890", {"start": v(-1.82, -9.2) * mm, "end": v(-1.71, -9.15) * mm});
            skLineSegment(sketch, "E891", {"start": v(-1.71, -9.15) * mm, "end": v(-1.6, -9.09) * mm});
            skLineSegment(sketch, "E892", {"start": v(-1.6, -9.09) * mm, "end": v(-1.5, -9.02) * mm});
            skLineSegment(sketch, "E893", {"start": v(-1.5, -9.02) * mm, "end": v(-1.41, -8.93) * mm});
            skLineSegment(sketch, "E894", {"start": v(-1.41, -8.93) * mm, "end": v(-1.33, -8.84) * mm});
            skLineSegment(sketch, "E895", {"start": v(-1.33, -8.84) * mm, "end": v(-1.26, -8.74) * mm});
            skLineSegment(sketch, "E896", {"start": v(-1.26, -8.74) * mm, "end": v(-1.2, -8.63) * mm});
            skLineSegment(sketch, "E897", {"start": v(-1.2, -8.63) * mm, "end": v(-1.14, -8.52) * mm});
            skLineSegment(sketch, "E898", {"start": v(-1.14, -8.52) * mm, "end": v(-1.1, -8.4) * mm});
            skLineSegment(sketch, "E899", {"start": v(-1.1, -8.4) * mm, "end": v(-1.06, -8.28) * mm});
            skLineSegment(sketch, "E900", {"start": v(-1.06, -8.28) * mm, "end": v(-1.04, -8.15) * mm});
            skLineSegment(sketch, "E901", {"start": v(-1.04, -8.15) * mm, "end": v(-1.03, -8.02) * mm});
            skLineSegment(sketch, "E902", {"start": v(-1.03, -8.02) * mm, "end": v(-1.03, -7.9) * mm});
            skLineSegment(sketch, "E903", {"start": v(-1.03, -7.9) * mm, "end": v(-1.03, -7.8) * mm});
            skLineSegment(sketch, "E904", {"start": v(-1.03, -7.8) * mm, "end": v(-1.03, -7.68) * mm});
            skLineSegment(sketch, "E905", {"start": v(-1.03, -7.68) * mm, "end": v(-1.03, -7.56) * mm});
            skLineSegment(sketch, "E906", {"start": v(-1.03, -7.56) * mm, "end": v(-1.03, -7.45) * mm});
            skLineSegment(sketch, "E907", {"start": v(-1.03, -7.45) * mm, "end": v(-1.03, -7.34) * mm});
            skLineSegment(sketch, "E908", {"start": v(-1.03, -7.34) * mm, "end": v(-1.03, -7.23) * mm});
            skLineSegment(sketch, "E909", {"start": v(-1.03, -7.23) * mm, "end": v(-1.03, -7.11) * mm});
            skLineSegment(sketch, "E910", {"start": v(-1.03, -7.11) * mm, "end": v(-1.03, -7) * mm});
            skLineSegment(sketch, "E911", {"start": v(-1.03, -7) * mm, "end": v(-1.03, -6.89) * mm});
            skLineSegment(sketch, "E912", {"start": v(-1.03, -6.89) * mm, "end": v(-1.03, -6.77) * mm});
            skLineSegment(sketch, "E913", {"start": v(-1.03, -6.77) * mm, "end": v(-1.03, -6.66) * mm});
            skLineSegment(sketch, "E914", {"start": v(-1.03, -6.66) * mm, "end": v(-1.03, -6.55) * mm});
            skLineSegment(sketch, "E915", {"start": v(-1.03, -6.55) * mm, "end": v(-1.03, -6.43) * mm});
            skLineSegment(sketch, "E916", {"start": v(-1.03, -6.43) * mm, "end": v(-1.03, -6.32) * mm});
            skLineSegment(sketch, "E917", {"start": v(-1.03, -6.32) * mm, "end": v(-1.03, -6.2) * mm});
            skLineSegment(sketch, "E918", {"start": v(-1.03, -6.2) * mm, "end": v(-0.97, -6.2) * mm});
            skLineSegment(sketch, "E919", {"start": v(-0.97, -6.2) * mm, "end": v(-0.9, -6.2) * mm});
            skLineSegment(sketch, "E920", {"start": v(-0.9, -6.2) * mm, "end": v(-0.84, -6.2) * mm});
            skLineSegment(sketch, "E921", {"start": v(-0.84, -6.2) * mm, "end": v(-0.78, -6.2) * mm});
            skLineSegment(sketch, "E922", {"start": v(-0.78, -6.2) * mm, "end": v(-0.71, -6.2) * mm});
            skLineSegment(sketch, "E923", {"start": v(-0.71, -6.2) * mm, "end": v(-0.65, -6.2) * mm});
            skLineSegment(sketch, "E924", {"start": v(-0.65, -6.2) * mm, "end": v(-0.58, -6.2) * mm});
            skLineSegment(sketch, "E925", {"start": v(-0.58, -6.2) * mm, "end": v(-0.52, -6.2) * mm});
            skLineSegment(sketch, "E926", {"start": v(-0.52, -6.2) * mm, "end": v(-0.45, -6.2) * mm});
            skLineSegment(sketch, "E927", {"start": v(-0.45, -6.2) * mm, "end": v(-0.39, -6.2) * mm});
            skLineSegment(sketch, "E928", {"start": v(-0.39, -6.2) * mm, "end": v(-0.32, -6.2) * mm});
            skLineSegment(sketch, "E929", {"start": v(-0.32, -6.2) * mm, "end": v(-0.26, -6.2) * mm});
            skLineSegment(sketch, "E930", {"start": v(-0.26, -6.2) * mm, "end": v(-0.2, -6.2) * mm});
            skLineSegment(sketch, "E931", {"start": v(-0.2, -6.2) * mm, "end": v(-0.13, -6.2) * mm});
            skLineSegment(sketch, "E932", {"start": v(-0.13, -6.2) * mm, "end": v(-0.06, -6.2) * mm});
            skLineSegment(sketch, "E933", {"start": v(-0.06, -6.2) * mm, "end": v(0, -6.2) * mm});
            skLineSegment(sketch, "E934", {"start": v(0, -6.2) * mm, "end": v(0.06, -6.2) * mm});
            skLineSegment(sketch, "E935", {"start": v(0.06, -6.2) * mm, "end": v(0.13, -6.2) * mm});
            skLineSegment(sketch, "E936", {"start": v(0.13, -6.2) * mm, "end": v(0.2, -6.2) * mm});
            skLineSegment(sketch, "E937", {"start": v(0.2, -6.2) * mm, "end": v(0.26, -6.2) * mm});
            skLineSegment(sketch, "E938", {"start": v(0.26, -6.2) * mm, "end": v(0.32, -6.2) * mm});
            skLineSegment(sketch, "E939", {"start": v(0.32, -6.2) * mm, "end": v(0.39, -6.2) * mm});
            skLineSegment(sketch, "E940", {"start": v(0.39, -6.2) * mm, "end": v(0.45, -6.2) * mm});
            skLineSegment(sketch, "E941", {"start": v(0.45, -6.2) * mm, "end": v(0.52, -6.2) * mm});
            skLineSegment(sketch, "E942", {"start": v(0.52, -6.2) * mm, "end": v(0.58, -6.2) * mm});
            skLineSegment(sketch, "E943", {"start": v(0.58, -6.2) * mm, "end": v(0.65, -6.2) * mm});
            skLineSegment(sketch, "E944", {"start": v(0.65, -6.2) * mm, "end": v(0.71, -6.2) * mm});
            skLineSegment(sketch, "E945", {"start": v(0.71, -6.2) * mm, "end": v(0.78, -6.2) * mm});
            skLineSegment(sketch, "E946", {"start": v(0.78, -6.2) * mm, "end": v(0.84, -6.2) * mm});
            skLineSegment(sketch, "E947", {"start": v(0.84, -6.2) * mm, "end": v(0.9, -6.2) * mm});
            skLineSegment(sketch, "E948", {"start": v(0.9, -6.2) * mm, "end": v(0.97, -6.2) * mm});
            skLineSegment(sketch, "E949", {"start": v(0.97, -6.2) * mm, "end": v(1.03, -6.2) * mm});
            skLineSegment(sketch, "E950", {"start": v(1.03, -6.2) * mm, "end": v(1.03, -6.32) * mm});
            skLineSegment(sketch, "E951", {"start": v(1.03, -6.32) * mm, "end": v(1.03, -6.43) * mm});
            skLineSegment(sketch, "E952", {"start": v(1.03, -6.43) * mm, "end": v(1.03, -6.55) * mm});
            skLineSegment(sketch, "E953", {"start": v(1.03, -6.55) * mm, "end": v(1.03, -6.66) * mm});
            skLineSegment(sketch, "E954", {"start": v(1.03, -6.66) * mm, "end": v(1.03, -6.77) * mm});
            skLineSegment(sketch, "E955", {"start": v(1.03, -6.77) * mm, "end": v(1.03, -6.89) * mm});
            skLineSegment(sketch, "E956", {"start": v(1.03, -6.89) * mm, "end": v(1.03, -7) * mm});
            skLineSegment(sketch, "E957", {"start": v(1.03, -7) * mm, "end": v(1.03, -7.11) * mm});
            skLineSegment(sketch, "E958", {"start": v(1.03, -7.11) * mm, "end": v(1.03, -7.23) * mm});
            skLineSegment(sketch, "E959", {"start": v(1.03, -7.23) * mm, "end": v(1.03, -7.34) * mm});
            skLineSegment(sketch, "E960", {"start": v(1.03, -7.34) * mm, "end": v(1.03, -7.45) * mm});
            skLineSegment(sketch, "E961", {"start": v(1.03, -7.45) * mm, "end": v(1.03, -7.56) * mm});
            skLineSegment(sketch, "E962", {"start": v(1.03, -7.56) * mm, "end": v(1.03, -7.68) * mm});
            skLineSegment(sketch, "E963", {"start": v(1.03, -7.68) * mm, "end": v(1.03, -7.8) * mm});
            skLineSegment(sketch, "E964", {"start": v(1.03, -7.8) * mm, "end": v(1.03, -7.9) * mm});
            skLineSegment(sketch, "E965", {"start": v(1.03, -7.9) * mm, "end": v(1.03, -8.02) * mm});
            skLineSegment(sketch, "E966", {"start": v(1.03, -8.02) * mm, "end": v(1.04, -8.15) * mm});
            skLineSegment(sketch, "E967", {"start": v(1.04, -8.15) * mm, "end": v(1.06, -8.28) * mm});
            skLineSegment(sketch, "E968", {"start": v(1.06, -8.28) * mm, "end": v(1.1, -8.4) * mm});
            skLineSegment(sketch, "E969", {"start": v(1.1, -8.4) * mm, "end": v(1.14, -8.52) * mm});
            skLineSegment(sketch, "E970", {"start": v(1.14, -8.52) * mm, "end": v(1.2, -8.63) * mm});
            skLineSegment(sketch, "E971", {"start": v(1.2, -8.63) * mm, "end": v(1.26, -8.74) * mm});
            skLineSegment(sketch, "E972", {"start": v(1.26, -8.74) * mm, "end": v(1.33, -8.84) * mm});
            skLineSegment(sketch, "E973", {"start": v(1.33, -8.84) * mm, "end": v(1.41, -8.93) * mm});
            skLineSegment(sketch, "E974", {"start": v(1.41, -8.93) * mm, "end": v(1.5, -9.02) * mm});
            skLineSegment(sketch, "E975", {"start": v(1.5, -9.02) * mm, "end": v(1.6, -9.09) * mm});
            skLineSegment(sketch, "E976", {"start": v(1.6, -9.09) * mm, "end": v(1.71, -9.15) * mm});
            skLineSegment(sketch, "E977", {"start": v(1.71, -9.15) * mm, "end": v(1.82, -9.2) * mm});
            skLineSegment(sketch, "E978", {"start": v(1.82, -9.2) * mm, "end": v(1.94, -9.25) * mm});
            skLineSegment(sketch, "E979", {"start": v(1.94, -9.25) * mm, "end": v(2.07, -9.28) * mm});
            skLineSegment(sketch, "E980", {"start": v(2.07, -9.28) * mm, "end": v(2.2, -9.3) * mm});
            skLineSegment(sketch, "E981", {"start": v(2.2, -9.3) * mm, "end": v(2.33, -9.31) * mm});
            skLineSegment(sketch, "E982", {"start": v(2.33, -9.31) * mm, "end": v(2.44, -9.31) * mm});
            skLineSegment(sketch, "E983", {"start": v(2.44, -9.31) * mm, "end": v(2.55, -9.31) * mm});
            skLineSegment(sketch, "E984", {"start": v(2.55, -9.31) * mm, "end": v(2.67, -9.31) * mm});
            skLineSegment(sketch, "E985", {"start": v(2.67, -9.31) * mm, "end": v(2.78, -9.31) * mm});
            skLineSegment(sketch, "E986", {"start": v(2.78, -9.31) * mm, "end": v(2.9, -9.31) * mm});
            skLineSegment(sketch, "E987", {"start": v(2.9, -9.31) * mm, "end": v(3, -9.31) * mm});
            skLineSegment(sketch, "E988", {"start": v(3, -9.31) * mm, "end": v(3.12, -9.31) * mm});
            skLineSegment(sketch, "E989", {"start": v(3.12, -9.31) * mm, "end": v(3.23, -9.31) * mm});
            skLineSegment(sketch, "E990", {"start": v(3.23, -9.31) * mm, "end": v(3.35, -9.31) * mm});
            skLineSegment(sketch, "E991", {"start": v(3.35, -9.31) * mm, "end": v(3.46, -9.31) * mm});
            skLineSegment(sketch, "E992", {"start": v(3.46, -9.31) * mm, "end": v(3.57, -9.31) * mm});
            skLineSegment(sketch, "E993", {"start": v(3.57, -9.31) * mm, "end": v(3.69, -9.31) * mm});
            skLineSegment(sketch, "E994", {"start": v(3.69, -9.31) * mm, "end": v(3.8, -9.31) * mm});
            skLineSegment(sketch, "E995", {"start": v(3.8, -9.31) * mm, "end": v(3.91, -9.31) * mm});
            skLineSegment(sketch, "E996", {"start": v(3.91, -9.31) * mm, "end": v(4.02, -9.31) * mm});
            skLineSegment(sketch, "E997", {"start": v(4.02, -9.31) * mm, "end": v(4.14, -9.31) * mm});
            skLineSegment(sketch, "E998", {"start": v(4.14, -9.31) * mm, "end": v(4.14, -9.44) * mm});
            skLineSegment(sketch, "E999", {"start": v(4.14, -9.44) * mm, "end": v(4.14, -9.57) * mm});
            skLineSegment(sketch, "E1000", {"start": v(4.14, -9.57) * mm, "end": v(4.14, -9.7) * mm});
            skLineSegment(sketch, "E1001", {"start": v(4.14, -9.7) * mm, "end": v(4.14, -9.83) * mm});
            skLineSegment(sketch, "E1002", {"start": v(4.14, -9.83) * mm, "end": v(4.14, -9.96) * mm});
            skLineSegment(sketch, "E1003", {"start": v(4.14, -9.96) * mm, "end": v(4.14, -10.09) * mm});
            skLineSegment(sketch, "E1004", {"start": v(4.14, -10.09) * mm, "end": v(4.14, -10.22) * mm});
            skLineSegment(sketch, "E1005", {"start": v(4.14, -10.22) * mm, "end": v(4.14, -10.34) * mm});
            skLineSegment(sketch, "E1006", {"start": v(4.14, -10.34) * mm, "end": v(4.14, -10.47) * mm});
            skLineSegment(sketch, "E1007", {"start": v(4.14, -10.47) * mm, "end": v(4.14, -10.6) * mm});
            skLineSegment(sketch, "E1008", {"start": v(4.14, -10.6) * mm, "end": v(4.14, -10.73) * mm});
            skLineSegment(sketch, "E1009", {"start": v(4.14, -10.73) * mm, "end": v(4.14, -10.86) * mm});
            skLineSegment(sketch, "E1010", {"start": v(4.14, -10.86) * mm, "end": v(4.14, -11) * mm});
            skLineSegment(sketch, "E1011", {"start": v(4.14, -11) * mm, "end": v(4.14, -11.12) * mm});
            skLineSegment(sketch, "E1012", {"start": v(4.14, -11.12) * mm, "end": v(4.14, -11.25) * mm});
            skLineSegment(sketch, "E1013", {"start": v(4.14, -11.25) * mm, "end": v(4.14, -11.38) * mm});
            skLineSegment(sketch, "E1014", {"start": v(4.14, -11.38) * mm, "end": v(4.14, -11.6) * mm});
            skLineSegment(sketch, "E1015", {"start": v(4.14, -11.6) * mm, "end": v(4.14, -11.83) * mm});
            skLineSegment(sketch, "E1016", {"start": v(4.14, -11.83) * mm, "end": v(4.14, -12.06) * mm});
            skLineSegment(sketch, "E1017", {"start": v(4.14, -12.06) * mm, "end": v(4.14, -12.28) * mm});
            skLineSegment(sketch, "E1018", {"start": v(4.14, -12.28) * mm, "end": v(4.14, -12.51) * mm});
            skLineSegment(sketch, "E1019", {"start": v(4.14, -12.51) * mm, "end": v(4.14, -12.74) * mm});
            skLineSegment(sketch, "E1020", {"start": v(4.14, -12.74) * mm, "end": v(4.14, -12.96) * mm});
            skLineSegment(sketch, "E1021", {"start": v(4.14, -12.96) * mm, "end": v(4.14, -13.19) * mm});
            skLineSegment(sketch, "E1022", {"start": v(4.14, -13.19) * mm, "end": v(4.14, -13.42) * mm});
            skLineSegment(sketch, "E1023", {"start": v(4.14, -13.42) * mm, "end": v(4.14, -13.64) * mm});
            skLineSegment(sketch, "E1024", {"start": v(4.14, -13.64) * mm, "end": v(4.14, -13.87) * mm});
            skLineSegment(sketch, "E1025", {"start": v(4.14, -13.87) * mm, "end": v(4.14, -14.1) * mm});
            skLineSegment(sketch, "E1026", {"start": v(4.14, -14.1) * mm, "end": v(4.14, -14.32) * mm});
            skLineSegment(sketch, "E1027", {"start": v(4.14, -14.32) * mm, "end": v(4.14, -14.55) * mm});
            skLineSegment(sketch, "E1028", {"start": v(4.14, -14.55) * mm, "end": v(4.14, -14.77) * mm});
            skLineSegment(sketch, "E1029", {"start": v(4.14, -14.77) * mm, "end": v(4.14, -15) * mm});
            skLineSegment(sketch, "E1030", {"start": v(4.14, -15) * mm, "end": v(4.27, -14.95) * mm});
            skLineSegment(sketch, "E1031", {"start": v(4.27, -14.95) * mm, "end": v(4.4, -14.9) * mm});
            skLineSegment(sketch, "E1032", {"start": v(4.4, -14.9) * mm, "end": v(4.53, -14.84) * mm});
            skLineSegment(sketch, "E1033", {"start": v(4.53, -14.84) * mm, "end": v(4.66, -14.8) * mm});
            skLineSegment(sketch, "E1034", {"start": v(4.66, -14.8) * mm, "end": v(4.78, -14.74) * mm});
            skLineSegment(sketch, "E1035", {"start": v(4.78, -14.74) * mm, "end": v(4.91, -14.69) * mm});
            skLineSegment(sketch, "E1036", {"start": v(4.91, -14.69) * mm, "end": v(5.04, -14.64) * mm});
            skLineSegment(sketch, "E1037", {"start": v(5.04, -14.64) * mm, "end": v(5.17, -14.59) * mm});
            skLineSegment(sketch, "E1038", {"start": v(5.17, -14.59) * mm, "end": v(5.3, -14.53) * mm});
            skLineSegment(sketch, "E1039", {"start": v(5.3, -14.53) * mm, "end": v(5.43, -14.48) * mm});
            skLineSegment(sketch, "E1040", {"start": v(5.43, -14.48) * mm, "end": v(5.56, -14.43) * mm});
            skLineSegment(sketch, "E1041", {"start": v(5.56, -14.43) * mm, "end": v(5.69, -14.38) * mm});
            skLineSegment(sketch, "E1042", {"start": v(5.69, -14.38) * mm, "end": v(5.82, -14.33) * mm});
            skLineSegment(sketch, "E1043", {"start": v(5.82, -14.33) * mm, "end": v(5.95, -14.28) * mm});
            skLineSegment(sketch, "E1044", {"start": v(5.95, -14.28) * mm, "end": v(6.08, -14.22) * mm});
            skLineSegment(sketch, "E1045", {"start": v(6.08, -14.22) * mm, "end": v(6.2, -14.17) * mm});
            skLineSegment(sketch, "E1046", {"start": v(6.2, -14.17) * mm, "end": v(6.24, -14.16) * mm});
            skLineSegment(sketch, "E1047", {"start": v(6.24, -14.16) * mm, "end": v(6.27, -14.15) * mm});
            skLineSegment(sketch, "E1048", {"start": v(6.27, -14.15) * mm, "end": v(6.3, -14.13) * mm});
            skLineSegment(sketch, "E1049", {"start": v(6.3, -14.13) * mm, "end": v(6.34, -14.12) * mm});
            skLineSegment(sketch, "E1050", {"start": v(6.34, -14.12) * mm, "end": v(6.37, -14.1) * mm});
            skLineSegment(sketch, "E1051", {"start": v(6.37, -14.1) * mm, "end": v(6.4, -14.1) * mm});
            skLineSegment(sketch, "E1052", {"start": v(6.4, -14.1) * mm, "end": v(6.43, -14.08) * mm});
            skLineSegment(sketch, "E1053", {"start": v(6.43, -14.08) * mm, "end": v(6.47, -14.07) * mm});
            skLineSegment(sketch, "E1054", {"start": v(6.47, -14.07) * mm, "end": v(6.5, -14.06) * mm});
            skLineSegment(sketch, "E1055", {"start": v(6.5, -14.06) * mm, "end": v(6.53, -14.04) * mm});
            skLineSegment(sketch, "E1056", {"start": v(6.53, -14.04) * mm, "end": v(6.56, -14.03) * mm});
            skLineSegment(sketch, "E1057", {"start": v(6.56, -14.03) * mm, "end": v(6.6, -14.02) * mm});
            skLineSegment(sketch, "E1058", {"start": v(6.6, -14.02) * mm, "end": v(6.63, -14) * mm});
            skLineSegment(sketch, "E1059", {"start": v(6.63, -14) * mm, "end": v(6.66, -14) * mm});
            skLineSegment(sketch, "E1060", {"start": v(6.66, -14) * mm, "end": v(6.7, -13.98) * mm});
            skLineSegment(sketch, "E1061", {"start": v(6.7, -13.98) * mm, "end": v(6.72, -13.97) * mm});
            skLineSegment(sketch, "E1062", {"start": v(6.72, -13.97) * mm, "end": v(6.86, -13.65) * mm});
            skLineSegment(sketch, "E1063", {"start": v(6.86, -13.65) * mm, "end": v(7, -13.33) * mm});
            skLineSegment(sketch, "E1064", {"start": v(7, -13.33) * mm, "end": v(7.12, -13) * mm});
            skLineSegment(sketch, "E1065", {"start": v(7.12, -13) * mm, "end": v(7.26, -12.69) * mm});
            skLineSegment(sketch, "E1066", {"start": v(7.26, -12.69) * mm, "end": v(7.39, -12.37) * mm});
            skLineSegment(sketch, "E1067", {"start": v(7.39, -12.37) * mm, "end": v(7.52, -12.05) * mm});
            skLineSegment(sketch, "E1068", {"start": v(7.52, -12.05) * mm, "end": v(7.66, -11.73) * mm});
            skLineSegment(sketch, "E1069", {"start": v(7.66, -11.73) * mm, "end": v(7.79, -11.4) * mm});
            skLineSegment(sketch, "E1070", {"start": v(7.79, -11.4) * mm, "end": v(7.92, -11.1) * mm});
            skLineSegment(sketch, "E1071", {"start": v(7.92, -11.1) * mm, "end": v(8.06, -10.77) * mm});
            skLineSegment(sketch, "E1072", {"start": v(8.06, -10.77) * mm, "end": v(8.19, -10.45) * mm});
            skLineSegment(sketch, "E1073", {"start": v(8.19, -10.45) * mm, "end": v(8.32, -10.13) * mm});
            skLineSegment(sketch, "E1074", {"start": v(8.32, -10.13) * mm, "end": v(8.45, -9.81) * mm});
            skLineSegment(sketch, "E1075", {"start": v(8.45, -9.81) * mm, "end": v(8.59, -9.5) * mm});
            skLineSegment(sketch, "E1076", {"start": v(8.59, -9.5) * mm, "end": v(8.72, -9.17) * mm});
            skLineSegment(sketch, "E1077", {"start": v(8.72, -9.17) * mm, "end": v(8.85, -8.85) * mm});
            skLineSegment(sketch, "E1078", {"start": v(8.85, -8.85) * mm, "end": v(9.17, -8.72) * mm});
            skLineSegment(sketch, "E1079", {"start": v(9.17, -8.72) * mm, "end": v(9.5, -8.59) * mm});
            skLineSegment(sketch, "E1080", {"start": v(9.5, -8.59) * mm, "end": v(9.81, -8.45) * mm});
            skLineSegment(sketch, "E1081", {"start": v(9.81, -8.45) * mm, "end": v(10.13, -8.32) * mm});
            skLineSegment(sketch, "E1082", {"start": v(10.13, -8.32) * mm, "end": v(10.45, -8.19) * mm});
            skLineSegment(sketch, "E1083", {"start": v(10.45, -8.19) * mm, "end": v(10.77, -8.06) * mm});
            skLineSegment(sketch, "E1084", {"start": v(10.77, -8.06) * mm, "end": v(11.1, -7.92) * mm});
            skLineSegment(sketch, "E1085", {"start": v(11.1, -7.92) * mm, "end": v(11.4, -7.79) * mm});
            skLineSegment(sketch, "E1086", {"start": v(11.4, -7.79) * mm, "end": v(11.73, -7.66) * mm});
            skLineSegment(sketch, "E1087", {"start": v(11.73, -7.66) * mm, "end": v(12.05, -7.52) * mm});
            skLineSegment(sketch, "E1088", {"start": v(12.05, -7.52) * mm, "end": v(12.37, -7.39) * mm});
            skLineSegment(sketch, "E1089", {"start": v(12.37, -7.39) * mm, "end": v(12.69, -7.26) * mm});
            skLineSegment(sketch, "E1090", {"start": v(12.69, -7.26) * mm, "end": v(13, -7.12) * mm});
            skLineSegment(sketch, "E1091", {"start": v(13, -7.12) * mm, "end": v(13.33, -7) * mm});
            skLineSegment(sketch, "E1092", {"start": v(13.33, -7) * mm, "end": v(13.65, -6.86) * mm});
            skLineSegment(sketch, "E1093", {"start": v(13.65, -6.86) * mm, "end": v(13.97, -6.72) * mm});
            skLineSegment(sketch, "E1094", {"start": v(13.97, -6.72) * mm, "end": v(13.98, -6.7) * mm});
            skLineSegment(sketch, "E1095", {"start": v(13.98, -6.7) * mm, "end": v(14, -6.66) * mm});
            skLineSegment(sketch, "E1096", {"start": v(14, -6.66) * mm, "end": v(14, -6.63) * mm});
            skLineSegment(sketch, "E1097", {"start": v(14, -6.63) * mm, "end": v(14.02, -6.6) * mm});
            skLineSegment(sketch, "E1098", {"start": v(14.02, -6.6) * mm, "end": v(14.03, -6.56) * mm});
            skLineSegment(sketch, "E1099", {"start": v(14.03, -6.56) * mm, "end": v(14.04, -6.53) * mm});
            skLineSegment(sketch, "E1100", {"start": v(14.04, -6.53) * mm, "end": v(14.06, -6.5) * mm});
            skLineSegment(sketch, "E1101", {"start": v(14.06, -6.5) * mm, "end": v(14.07, -6.47) * mm});
            skLineSegment(sketch, "E1102", {"start": v(14.07, -6.47) * mm, "end": v(14.08, -6.43) * mm});
            skLineSegment(sketch, "E1103", {"start": v(14.08, -6.43) * mm, "end": v(14.1, -6.4) * mm});
            skLineSegment(sketch, "E1104", {"start": v(14.1, -6.4) * mm, "end": v(14.1, -6.37) * mm});
            skLineSegment(sketch, "E1105", {"start": v(14.1, -6.37) * mm, "end": v(14.12, -6.34) * mm});
            skLineSegment(sketch, "E1106", {"start": v(14.12, -6.34) * mm, "end": v(14.13, -6.3) * mm});
            skLineSegment(sketch, "E1107", {"start": v(14.13, -6.3) * mm, "end": v(14.15, -6.27) * mm});
            skLineSegment(sketch, "E1108", {"start": v(14.15, -6.27) * mm, "end": v(14.16, -6.24) * mm});
            skLineSegment(sketch, "E1109", {"start": v(14.16, -6.24) * mm, "end": v(14.17, -6.2) * mm});
            skLineSegment(sketch, "E1110", {"start": v(14.17, -6.2) * mm, "end": v(14.22, -6.08) * mm});
            skLineSegment(sketch, "E1111", {"start": v(14.22, -6.08) * mm, "end": v(14.28, -5.95) * mm});
            skLineSegment(sketch, "E1112", {"start": v(14.28, -5.95) * mm, "end": v(14.33, -5.82) * mm});
            skLineSegment(sketch, "E1113", {"start": v(14.33, -5.82) * mm, "end": v(14.38, -5.69) * mm});
            skLineSegment(sketch, "E1114", {"start": v(14.38, -5.69) * mm, "end": v(14.43, -5.56) * mm});
            skLineSegment(sketch, "E1115", {"start": v(14.43, -5.56) * mm, "end": v(14.48, -5.43) * mm});
            skLineSegment(sketch, "E1116", {"start": v(14.48, -5.43) * mm, "end": v(14.53, -5.3) * mm});
            skLineSegment(sketch, "E1117", {"start": v(14.53, -5.3) * mm, "end": v(14.59, -5.17) * mm});
            skLineSegment(sketch, "E1118", {"start": v(14.59, -5.17) * mm, "end": v(14.64, -5.04) * mm});
            skLineSegment(sketch, "E1119", {"start": v(14.64, -5.04) * mm, "end": v(14.69, -4.91) * mm});
            skLineSegment(sketch, "E1120", {"start": v(14.69, -4.91) * mm, "end": v(14.74, -4.78) * mm});
            skLineSegment(sketch, "E1121", {"start": v(14.74, -4.78) * mm, "end": v(14.8, -4.66) * mm});
            skLineSegment(sketch, "E1122", {"start": v(14.8, -4.66) * mm, "end": v(14.84, -4.53) * mm});
            skLineSegment(sketch, "E1123", {"start": v(14.84, -4.53) * mm, "end": v(14.9, -4.4) * mm});
            skLineSegment(sketch, "E1124", {"start": v(14.9, -4.4) * mm, "end": v(14.95, -4.27) * mm});
            skLineSegment(sketch, "E1125", {"start": v(14.95, -4.27) * mm, "end": v(15, -4.14) * mm});
            skLineSegment(sketch, "E1126", {"start": v(15, -4.14) * mm, "end": v(14.77, -4.14) * mm});
            skLineSegment(sketch, "E1127", {"start": v(14.77, -4.14) * mm, "end": v(14.55, -4.14) * mm});
            skLineSegment(sketch, "E1128", {"start": v(14.55, -4.14) * mm, "end": v(14.32, -4.14) * mm});
            skLineSegment(sketch, "E1129", {"start": v(14.32, -4.14) * mm, "end": v(14.1, -4.14) * mm});
            skLineSegment(sketch, "E1130", {"start": v(14.1, -4.14) * mm, "end": v(13.87, -4.14) * mm});
            skLineSegment(sketch, "E1131", {"start": v(13.87, -4.14) * mm, "end": v(13.64, -4.14) * mm});
            skLineSegment(sketch, "E1132", {"start": v(13.64, -4.14) * mm, "end": v(13.42, -4.14) * mm});
            skLineSegment(sketch, "E1133", {"start": v(13.42, -4.14) * mm, "end": v(13.19, -4.14) * mm});
            skLineSegment(sketch, "E1134", {"start": v(13.19, -4.14) * mm, "end": v(12.96, -4.14) * mm});
            skLineSegment(sketch, "E1135", {"start": v(12.96, -4.14) * mm, "end": v(12.74, -4.14) * mm});
            skLineSegment(sketch, "E1136", {"start": v(12.74, -4.14) * mm, "end": v(12.51, -4.14) * mm});
            skLineSegment(sketch, "E1137", {"start": v(12.51, -4.14) * mm, "end": v(12.28, -4.14) * mm});
            skLineSegment(sketch, "E1138", {"start": v(12.28, -4.14) * mm, "end": v(12.06, -4.14) * mm});
            skLineSegment(sketch, "E1139", {"start": v(12.06, -4.14) * mm, "end": v(11.83, -4.14) * mm});
            skLineSegment(sketch, "E1140", {"start": v(11.83, -4.14) * mm, "end": v(11.6, -4.14) * mm});
            skLineSegment(sketch, "E1141", {"start": v(11.6, -4.14) * mm, "end": v(11.38, -4.14) * mm});
            skLineSegment(sketch, "E1142", {"start": v(11.38, -4.14) * mm, "end": v(11.25, -4.14) * mm});
            skLineSegment(sketch, "E1143", {"start": v(11.25, -4.14) * mm, "end": v(11.12, -4.14) * mm});
            skLineSegment(sketch, "E1144", {"start": v(11.12, -4.14) * mm, "end": v(11, -4.14) * mm});
            skLineSegment(sketch, "E1145", {"start": v(11, -4.14) * mm, "end": v(10.86, -4.14) * mm});
            skLineSegment(sketch, "E1146", {"start": v(10.86, -4.14) * mm, "end": v(10.73, -4.14) * mm});
            skLineSegment(sketch, "E1147", {"start": v(10.73, -4.14) * mm, "end": v(10.6, -4.14) * mm});
            skLineSegment(sketch, "E1148", {"start": v(10.6, -4.14) * mm, "end": v(10.47, -4.14) * mm});
            skLineSegment(sketch, "E1149", {"start": v(10.47, -4.14) * mm, "end": v(10.34, -4.14) * mm});
            skLineSegment(sketch, "E1150", {"start": v(10.34, -4.14) * mm, "end": v(10.22, -4.14) * mm});
            skLineSegment(sketch, "E1151", {"start": v(10.22, -4.14) * mm, "end": v(10.09, -4.14) * mm});
            skLineSegment(sketch, "E1152", {"start": v(10.09, -4.14) * mm, "end": v(9.96, -4.14) * mm});
            skLineSegment(sketch, "E1153", {"start": v(9.96, -4.14) * mm, "end": v(9.83, -4.14) * mm});
            skLineSegment(sketch, "E1154", {"start": v(9.83, -4.14) * mm, "end": v(9.7, -4.14) * mm});
            skLineSegment(sketch, "E1155", {"start": v(9.7, -4.14) * mm, "end": v(9.57, -4.14) * mm});
            skLineSegment(sketch, "E1156", {"start": v(9.57, -4.14) * mm, "end": v(9.44, -4.14) * mm});
            skLineSegment(sketch, "E1157", {"start": v(9.44, -4.14) * mm, "end": v(9.31, -4.14) * mm});
            skLineSegment(sketch, "E1158", {"start": v(-1.03, -1.03) * mm, "end": v(-1.03, -0.9) * mm});
            skLineSegment(sketch, "E1159", {"start": v(-1.03, -0.9) * mm, "end": v(-1.03, -0.78) * mm});
            skLineSegment(sketch, "E1160", {"start": v(-1.03, -0.78) * mm, "end": v(-1.03, -0.65) * mm});
            skLineSegment(sketch, "E1161", {"start": v(-1.03, -0.65) * mm, "end": v(-1.03, -0.52) * mm});
            skLineSegment(sketch, "E1162", {"start": v(-1.03, -0.52) * mm, "end": v(-1.03, -0.39) * mm});
            skLineSegment(sketch, "E1163", {"start": v(-1.03, -0.39) * mm, "end": v(-1.03, -0.26) * mm});
            skLineSegment(sketch, "E1164", {"start": v(-1.03, -0.26) * mm, "end": v(-1.03, -0.13) * mm});
            skLineSegment(sketch, "E1165", {"start": v(-1.03, -0.13) * mm, "end": v(-1.03, 0) * mm});
            skLineSegment(sketch, "E1166", {"start": v(-1.03, 0) * mm, "end": v(-1.03, 0.13) * mm});
            skLineSegment(sketch, "E1167", {"start": v(-1.03, 0.13) * mm, "end": v(-1.03, 0.26) * mm});
            skLineSegment(sketch, "E1168", {"start": v(-1.03, 0.26) * mm, "end": v(-1.03, 0.39) * mm});
            skLineSegment(sketch, "E1169", {"start": v(-1.03, 0.39) * mm, "end": v(-1.03, 0.52) * mm});
            skLineSegment(sketch, "E1170", {"start": v(-1.03, 0.52) * mm, "end": v(-1.03, 0.65) * mm});
            skLineSegment(sketch, "E1171", {"start": v(-1.03, 0.65) * mm, "end": v(-1.03, 0.78) * mm});
            skLineSegment(sketch, "E1172", {"start": v(-1.03, 0.78) * mm, "end": v(-1.03, 0.9) * mm});
            skLineSegment(sketch, "E1173", {"start": v(-1.03, 0.9) * mm, "end": v(-1.03, 1.03) * mm});
            skLineSegment(sketch, "E1174", {"start": v(-1.03, 1.03) * mm, "end": v(-0.9, 1.03) * mm});
            skLineSegment(sketch, "E1175", {"start": v(-0.9, 1.03) * mm, "end": v(-0.78, 1.03) * mm});
            skLineSegment(sketch, "E1176", {"start": v(-0.78, 1.03) * mm, "end": v(-0.65, 1.03) * mm});
            skLineSegment(sketch, "E1177", {"start": v(-0.65, 1.03) * mm, "end": v(-0.52, 1.03) * mm});
            skLineSegment(sketch, "E1178", {"start": v(-0.52, 1.03) * mm, "end": v(-0.39, 1.03) * mm});
            skLineSegment(sketch, "E1179", {"start": v(-0.39, 1.03) * mm, "end": v(-0.26, 1.03) * mm});
            skLineSegment(sketch, "E1180", {"start": v(-0.26, 1.03) * mm, "end": v(-0.13, 1.03) * mm});
            skLineSegment(sketch, "E1181", {"start": v(-0.13, 1.03) * mm, "end": v(0, 1.03) * mm});
            skLineSegment(sketch, "E1182", {"start": v(0, 1.03) * mm, "end": v(0.13, 1.03) * mm});
            skLineSegment(sketch, "E1183", {"start": v(0.13, 1.03) * mm, "end": v(0.26, 1.03) * mm});
            skLineSegment(sketch, "E1184", {"start": v(0.26, 1.03) * mm, "end": v(0.39, 1.03) * mm});
            skLineSegment(sketch, "E1185", {"start": v(0.39, 1.03) * mm, "end": v(0.52, 1.03) * mm});
            skLineSegment(sketch, "E1186", {"start": v(0.52, 1.03) * mm, "end": v(0.65, 1.03) * mm});
            skLineSegment(sketch, "E1187", {"start": v(0.65, 1.03) * mm, "end": v(0.78, 1.03) * mm});
            skLineSegment(sketch, "E1188", {"start": v(0.78, 1.03) * mm, "end": v(0.9, 1.03) * mm});
            skLineSegment(sketch, "E1189", {"start": v(0.9, 1.03) * mm, "end": v(1.03, 1.03) * mm});
            skLineSegment(sketch, "E1190", {"start": v(1.03, 1.03) * mm, "end": v(1.03, 0.9) * mm});
            skLineSegment(sketch, "E1191", {"start": v(1.03, 0.9) * mm, "end": v(1.03, 0.78) * mm});
            skLineSegment(sketch, "E1192", {"start": v(1.03, 0.78) * mm, "end": v(1.03, 0.65) * mm});
            skLineSegment(sketch, "E1193", {"start": v(1.03, 0.65) * mm, "end": v(1.03, 0.52) * mm});
            skLineSegment(sketch, "E1194", {"start": v(1.03, 0.52) * mm, "end": v(1.03, 0.39) * mm});
            skLineSegment(sketch, "E1195", {"start": v(1.03, 0.39) * mm, "end": v(1.03, 0.26) * mm});
            skLineSegment(sketch, "E1196", {"start": v(1.03, 0.26) * mm, "end": v(1.03, 0.13) * mm});
            skLineSegment(sketch, "E1197", {"start": v(1.03, 0.13) * mm, "end": v(1.03, 0) * mm});
            skLineSegment(sketch, "E1198", {"start": v(1.03, 0) * mm, "end": v(1.03, -0.13) * mm});
            skLineSegment(sketch, "E1199", {"start": v(1.03, -0.13) * mm, "end": v(1.03, -0.26) * mm});
            skLineSegment(sketch, "E1200", {"start": v(1.03, -0.26) * mm, "end": v(1.03, -0.39) * mm});
            skLineSegment(sketch, "E1201", {"start": v(1.03, -0.39) * mm, "end": v(1.03, -0.52) * mm});
            skLineSegment(sketch, "E1202", {"start": v(1.03, -0.52) * mm, "end": v(1.03, -0.65) * mm});
            skLineSegment(sketch, "E1203", {"start": v(1.03, -0.65) * mm, "end": v(1.03, -0.78) * mm});
            skLineSegment(sketch, "E1204", {"start": v(1.03, -0.78) * mm, "end": v(1.03, -0.9) * mm});
            skLineSegment(sketch, "E1205", {"start": v(1.03, -0.9) * mm, "end": v(1.03, -1.03) * mm});
            skLineSegment(sketch, "E1206", {"start": v(1.03, -1.03) * mm, "end": v(0.9, -1.03) * mm});
            skLineSegment(sketch, "E1207", {"start": v(0.9, -1.03) * mm, "end": v(0.78, -1.03) * mm});
            skLineSegment(sketch, "E1208", {"start": v(0.78, -1.03) * mm, "end": v(0.65, -1.03) * mm});
            skLineSegment(sketch, "E1209", {"start": v(0.65, -1.03) * mm, "end": v(0.52, -1.03) * mm});
            skLineSegment(sketch, "E1210", {"start": v(0.52, -1.03) * mm, "end": v(0.39, -1.03) * mm});
            skLineSegment(sketch, "E1211", {"start": v(0.39, -1.03) * mm, "end": v(0.26, -1.03) * mm});
            skLineSegment(sketch, "E1212", {"start": v(0.26, -1.03) * mm, "end": v(0.13, -1.03) * mm});
            skLineSegment(sketch, "E1213", {"start": v(0.13, -1.03) * mm, "end": v(0, -1.03) * mm});
            skLineSegment(sketch, "E1214", {"start": v(0, -1.03) * mm, "end": v(-0.13, -1.03) * mm});
            skLineSegment(sketch, "E1215", {"start": v(-0.13, -1.03) * mm, "end": v(-0.26, -1.03) * mm});
            skLineSegment(sketch, "E1216", {"start": v(-0.26, -1.03) * mm, "end": v(-0.39, -1.03) * mm});
            skLineSegment(sketch, "E1217", {"start": v(-0.39, -1.03) * mm, "end": v(-0.52, -1.03) * mm});
            skLineSegment(sketch, "E1218", {"start": v(-0.52, -1.03) * mm, "end": v(-0.65, -1.03) * mm});
            skLineSegment(sketch, "E1219", {"start": v(-0.65, -1.03) * mm, "end": v(-0.78, -1.03) * mm});
            skLineSegment(sketch, "E1220", {"start": v(-0.78, -1.03) * mm, "end": v(-0.9, -1.03) * mm});
            skLineSegment(sketch, "E1221", {"start": v(-0.9, -1.03) * mm, "end": v(-1.03, -1.03) * mm});
            skLineSegment(sketch, "E1222.bottom", {"start": v(-1.47, 1.5) * mm, "end": v(1.45, 1.5) * mm});
            skLineSegment(sketch, "E1222.top", {"start": v(-1.47, -1.45) * mm, "end": v(1.45, -1.45) * mm});
            skLineSegment(sketch, "E1222.left", {"start": v(-1.47, 1.5) * mm, "end": v(-1.47, -1.45) * mm});
            skLineSegment(sketch, "E1222.right", {"start": v(1.45, 1.5) * mm, "end": v(1.45, -1.45) * mm});
            skSolve(sketch);
        }
        {
            var Q0;
            Q0=makeQuery(id+"F3.imprint","IMPRINT",FACE,{"disambiguationData":[TD([[makeQuery(id+"F3.imprint","IMPRINT",EDGE,{"derivedFrom":sQuery(id+"F3.wireOp",EDGE,"E6")}),1.0]])]});
            var Q1;
            Q1=makeQuery(id+"F3.imprint","IMPRINT",FACE,{"disambiguationData":[TD([[makeQuery(id+"F3.imprint","IMPRINT",EDGE,{"derivedFrom":sQuery(id+"F3.wireOp",EDGE,"E1158")}),1.0]])]});
            var Q2;
            Q2=makeQuery(id+"F3.imprint","IMPRINT",FACE,{"disambiguationData":[TD([[makeQuery(id+"F3.imprint","IMPRINT",EDGE,{"derivedFrom":sQuery(id+"F3.wireOp",EDGE,"E1158")}),-1.0]])]});
            extrude(context, id + "F4", {"entities" : qUnion([Q0, Q1, Q2]), "operationType" : NewBodyOperationType.REMOVE, "endBound" : BoundingType.THROUGH_ALL, "oppositeDirection" : true, "depth" : 25 * mm, "offsetDistance" : 25 * mm});
        }
        {
            var Q0;
            Q0=qCreatedBy(makeId("Front.planeOp"),FACE);
            var sketch = newSketch(context, id + "F5", { "sketchPlane" : qUnion([Q0])});
            skCircle(sketch, "E1223", {"center": v(-15, 5) * mm, "radius": 3.5 * mm});
            skLineSegment(sketch, "E1224", {"start": v(-17.89, 3.02) * mm, "end": v(-15.82, 0) * mm});
            skLineSegment(sketch, "E1225", {"start": v(-16.82, 0) * mm, "end": v(-18.21, 1.17) * mm, "construction": true});
            skLineSegment(sketch, "E1226", {"start": v(-12.32, 2.75) * mm, "end": v(-14.63, 0) * mm});
            skLineSegment(sketch, "E1227", {"start": v(-15.82, 0) * mm, "end": v(-14.63, 0) * mm});
            skSolve(sketch);
        }
        {
            var Q0;
            Q0=qSketchRegion(id+"F5",true);
            var Q1;
            Q1=sQuery(id+"F0.wireOp",EDGE,"E3");
            revolve(context, id + "F6", {"operationType" : NewBodyOperationType.ADD, "surfaceOperationType" : NewSurfaceOperationType.NEW, "entities" : qUnion([Q0]), "axis" : qUnion([Q1]), "revolveType" : RevolveType.FULL});
        }
        {
            var Q0;
            Q0=qCreatedBy(makeId("Top.planeOp"),FACE);
            var sketch = newSketch(context, id + "F7", { "sketchPlane" : qUnion([Q0])});
            skCircle(sketch, "E1228", {"center": v(0, 21) * mm, "radius": 4 * mm});
            skSolve(sketch);
        }
        {
            var Q0;
            Q0=makeQuery(id+"F7.imprint","IMPRINT",FACE,{"disambiguationData":[TD([[makeQuery(id+"F7.imprint","IMPRINT",EDGE,{"derivedFrom":sQuery(id+"F7.wireOp",EDGE,"E1228")}),1.0]])]});
            extrude(context, id + "F8", {"entities" : qUnion([Q0]), "operationType" : NewBodyOperationType.REMOVE, "depth" : 25 * mm, "offsetDistance" : 25 * mm});
        }
        {
            var Q0;
            Q0=makeQuery(id+"F8.boolean.opBoolean","INTERSECT",EDGE,{"derivedFrom":[makeQuery(id+"F4.boolean.opBoolean","SPLIT",FACE,{"disambiguationData":[TD([makeQuery(id+"F1.opRevolve","SWEPT_FACE",FACE,{"disambiguationData":[OSD([sQuery(id+"F0.wireOp",EDGE,"E2")])]}),makeQuery(id+"F4.opExtrude","SWEPT_FACE",FACE,{"disambiguationData":[OSD([sQuery(id+"F3.wireOp",EDGE,"705da5c4-06c6-4740-92ce-35b712dfc936.0")])]}),makeQuery(id+"F4.opExtrude","SWEPT_FACE",FACE,{"disambiguationData":[OSD([sQuery(id+"F3.wireOp",EDGE,"705da5c4-06c6-4740-92ce-35b712dfc936.1")])]}),makeQuery(id+"F4.opExtrude","SWEPT_FACE",FACE,{"disambiguationData":[OSD([sQuery(id+"F3.wireOp",EDGE,"705da5c4-06c6-4740-92ce-35b712dfc936.2")])]}),makeQuery(id+"F4.opExtrude","SWEPT_FACE",FACE,{"disambiguationData":[OSD([sQuery(id+"F3.wireOp",EDGE,"705da5c4-06c6-4740-92ce-35b712dfc936.3")])]}),makeQuery(id+"F4.opExtrude","SWEPT_FACE",FACE,{"disambiguationData":[OSD([sQuery(id+"F3.wireOp",EDGE,"705da5c4-06c6-4740-92ce-35b712dfc936.4")])]}),makeQuery(id+"F4.opExtrude","SWEPT_FACE",FACE,{"disambiguationData":[OSD([sQuery(id+"F3.wireOp",EDGE,"705da5c4-06c6-4740-92ce-35b712dfc936.5")])]})])],"derivedFrom":makeQuery(id+"F1.opRevolve","SWEPT_FACE",FACE,{"disambiguationData":[OSD([sQuery(id+"F0.wireOp",EDGE,"E1")])]})}),makeQuery(id+"F8.opExtrude","SWEPT_FACE",FACE,{"disambiguationData":[OSD([sQuery(id+"F7.wireOp",EDGE,"E1228")])]})]});
            fillet(context, id + "F9", {"entities" : qUnion([Q0]), "radius" : 1 * mm, "tangentPropagation" : true, "allowEdgeOverflow" : false});
        }
    });
